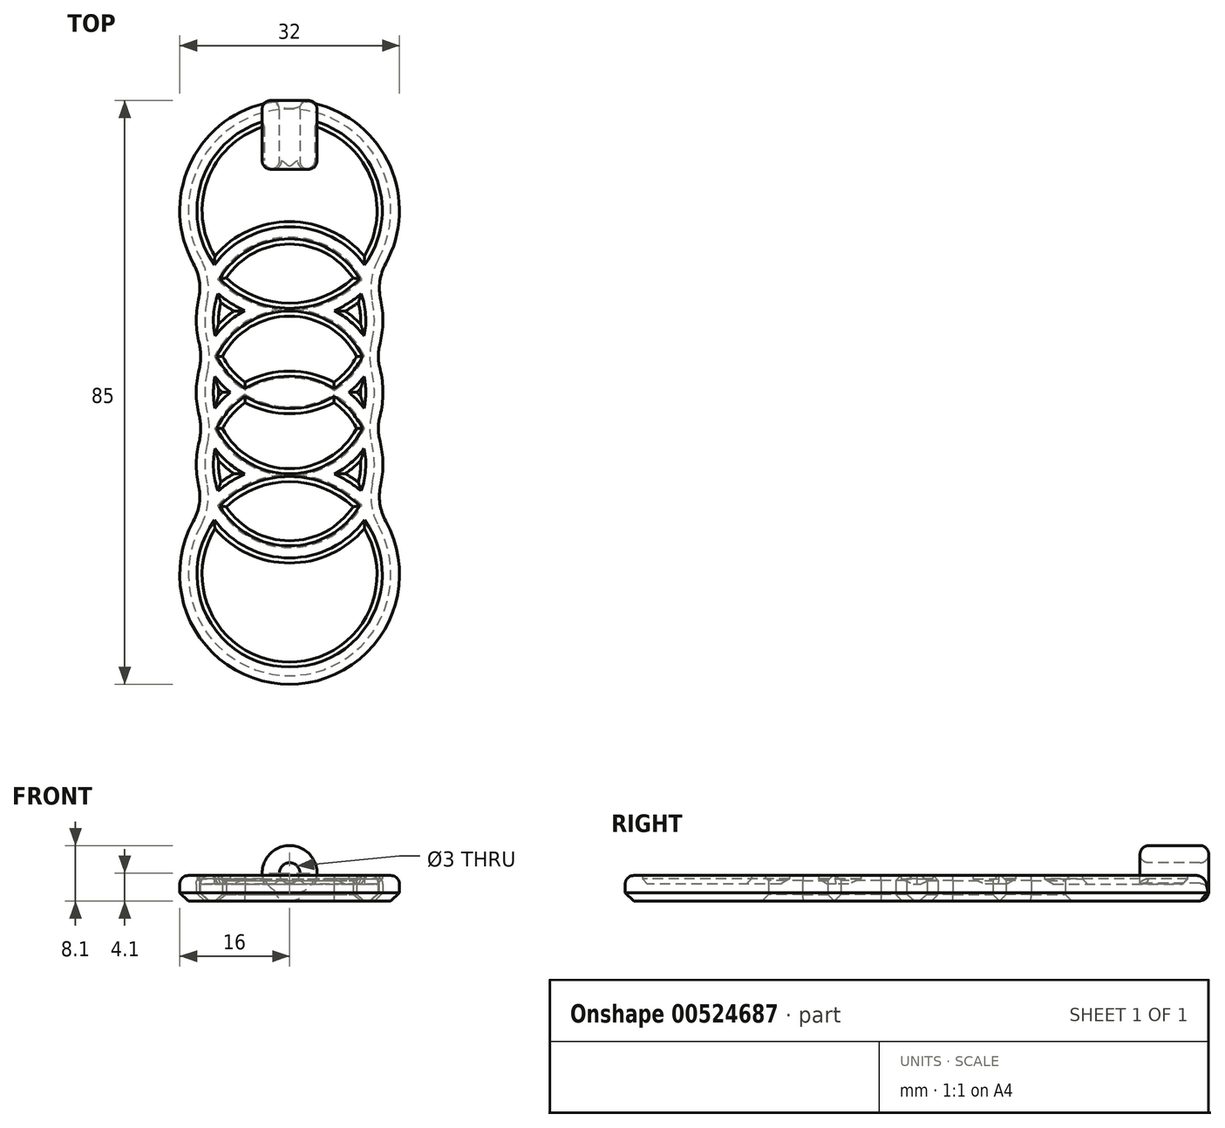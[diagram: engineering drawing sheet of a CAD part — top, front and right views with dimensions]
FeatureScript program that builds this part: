
annotation { "Feature Type Name" : "Feature", "Feature Type Description" : "" }
export const myFeature = defineFeature(function(context is Context, id is Id, definition is map)
    precondition{}
    {
        {
            assignVariable(context, id + "F0", {"name" : "thickness", "anyValue" : 2.5});
        }
        {
            assignVariable(context, id + "F1", {"name" : "handle_length", "anyValue" : 85});
        }
        {
            var Q0;
            Q0=qCreatedBy(makeId("Top.planeOp"),FACE);
            var sketch = newSketch(context, id + "F2", { "sketchPlane" : qUnion([Q0])});
            skLineSegment(sketch, "E0", {"start": v(0, -26.5) * mm, "end": v(0, 26.5) * mm, "construction": true});
            skCircle(sketch, "E1", {"center": v(0, 26.5) * mm, "radius": 16 * mm});
            skCircle(sketch, "E2", {"center": v(0, -26.5) * mm, "radius": 16 * mm});
            skCircle(sketch, "E3", {"center": v(0, 10.5) * mm, "radius": 13.6 * mm});
            skCircle(sketch, "E4", {"center": v(0, -10.5) * mm, "radius": 13.6 * mm});
            skCircle(sketch, "E5", {"center": v(0, 0) * mm, "radius": 13.6 * mm});
            skCircle(sketch, "E6.0", {"center": v(0, 26.5) * mm, "radius": 13.5 * mm});
            skCircle(sketch, "E7.0", {"center": v(0, 10.5) * mm, "radius": 11.1 * mm});
            skCircle(sketch, "E8.0", {"center": v(0, 0) * mm, "radius": 11.1 * mm});
            skCircle(sketch, "E9.0", {"center": v(0, -10.5) * mm, "radius": 11.1 * mm});
            skCircle(sketch, "E10.0", {"center": v(0, -26.5) * mm, "radius": 13.5 * mm});
            skSolve(sketch);
        }
        {
            var Q0;
            Q0=qCreatedBy(makeId("Front.planeOp"),FACE);
            var sketch = newSketch(context, id + "F3", { "sketchPlane" : qUnion([Q0])});
            skLineSegment(sketch, "E11", {"start": v(0, 0) * mm, "end": v(0, 4.1) * mm});
            skCircle(sketch, "E12", {"center": v(0, 4.1) * mm, "radius": 1.5 * mm});
            skCircle(sketch, "E13.0", {"center": v(0, 4.1) * mm, "radius": 4 * mm});
            skSolve(sketch);
        }
        {
            var Q0;
            {var subQ0=sQuery(id+"F2.wireOp",EDGE,"E4");var subQ1=sQuery(id+"F2.wireOp",EDGE,"E2");var subQ2=makeQuery(id+"F2.imprint","INTERSECT",VERTEX,{"disambiguationData":[OD(0.0)],"derivedFrom":[subQ1,subQ0]});Q0=makeQuery(id+"F2.imprint","IMPRINT",FACE,{"disambiguationData":[TD([[makeQuery(id+"F2.imprint","IMPRINT",EDGE,{"disambiguationData":[TD([[subQ2,-1.0]])],"derivedFrom":subQ1}),1.0]])]});}
            var Q1;
            {var subQ0=sQuery(id+"F2.wireOp",EDGE,"E4");var subQ1=sQuery(id+"F2.wireOp",EDGE,"E2");var subQ2=makeQuery(id+"F2.imprint","INTERSECT",VERTEX,{"disambiguationData":[OD(0.0)],"derivedFrom":[subQ1,subQ0]});Q1=makeQuery(id+"F2.imprint","IMPRINT",FACE,{"disambiguationData":[TD([[makeQuery(id+"F2.imprint","IMPRINT",EDGE,{"disambiguationData":[TD([[subQ2,1.0]])],"derivedFrom":subQ1}),1.0]])]});}
            var Q2;
            {var subQ0=sQuery(id+"F2.wireOp",EDGE,"E4");var subQ1=sQuery(id+"F2.wireOp",EDGE,"E2");var subQ2=makeQuery(id+"F2.imprint","INTERSECT",VERTEX,{"disambiguationData":[OD(0.0)],"derivedFrom":[subQ1,subQ0]});Q2=makeQuery(id+"F2.imprint","IMPRINT",FACE,{"disambiguationData":[TD([[makeQuery(id+"F2.imprint","IMPRINT",EDGE,{"disambiguationData":[TD([[subQ2,1.0]])],"derivedFrom":subQ1}),-1.0]])]});}
            var Q3;
            {var subQ0=sQuery(id+"F2.wireOp",EDGE,"E5");var subQ1=sQuery(id+"F2.wireOp",EDGE,"E4");var subQ2=makeQuery(id+"F2.imprint","INTERSECT",VERTEX,{"disambiguationData":[OD(0.0)],"derivedFrom":[subQ1,subQ0]});Q3=makeQuery(id+"F2.imprint","IMPRINT",FACE,{"disambiguationData":[TD([[makeQuery(id+"F2.imprint","IMPRINT",EDGE,{"disambiguationData":[TD([[subQ2,1.0]])],"derivedFrom":subQ1}),1.0]])]});}
            var Q4;
            {var subQ0=sQuery(id+"F2.wireOp",EDGE,"E5");var subQ1=sQuery(id+"F2.wireOp",EDGE,"E3");var subQ2=makeQuery(id+"F2.imprint","INTERSECT",VERTEX,{"disambiguationData":[OD(0.0)],"derivedFrom":[subQ1,subQ0]});Q4=makeQuery(id+"F2.imprint","IMPRINT",FACE,{"disambiguationData":[TD([[makeQuery(id+"F2.imprint","IMPRINT",EDGE,{"disambiguationData":[TD([[subQ2,-1.0]])],"derivedFrom":subQ1}),-1.0]])]});}
            var Q5;
            {var subQ0=sQuery(id+"F2.wireOp",EDGE,"E5");var subQ1=sQuery(id+"F2.wireOp",EDGE,"E3");var subQ2=makeQuery(id+"F2.imprint","INTERSECT",VERTEX,{"disambiguationData":[OD(0.0)],"derivedFrom":[subQ1,subQ0]});Q5=makeQuery(id+"F2.imprint","IMPRINT",FACE,{"disambiguationData":[TD([[makeQuery(id+"F2.imprint","IMPRINT",EDGE,{"disambiguationData":[TD([[subQ2,-1.0]])],"derivedFrom":subQ1}),1.0]])]});}
            var Q6;
            {var subQ0=sQuery(id+"F2.wireOp",EDGE,"E3");var subQ1=sQuery(id+"F2.wireOp",EDGE,"E1");var subQ2=makeQuery(id+"F2.imprint","INTERSECT",VERTEX,{"disambiguationData":[OD(0.0)],"derivedFrom":[subQ1,subQ0]});Q6=makeQuery(id+"F2.imprint","IMPRINT",FACE,{"disambiguationData":[TD([[makeQuery(id+"F2.imprint","IMPRINT",EDGE,{"disambiguationData":[TD([[subQ2,-1.0]])],"derivedFrom":subQ1}),-1.0]])]});}
            var Q7;
            {var subQ0=sQuery(id+"F2.wireOp",EDGE,"E3");var subQ1=sQuery(id+"F2.wireOp",EDGE,"E1");var subQ2=makeQuery(id+"F2.imprint","INTERSECT",VERTEX,{"disambiguationData":[OD(0.0)],"derivedFrom":[subQ1,subQ0]});Q7=makeQuery(id+"F2.imprint","IMPRINT",FACE,{"disambiguationData":[TD([[makeQuery(id+"F2.imprint","IMPRINT",EDGE,{"disambiguationData":[TD([[subQ2,-1.0]])],"derivedFrom":subQ1}),1.0]])]});}
            var Q8;
            {var subQ0=sQuery(id+"F2.wireOp",EDGE,"E3");var subQ1=sQuery(id+"F2.wireOp",EDGE,"E1");var subQ2=makeQuery(id+"F2.imprint","INTERSECT",VERTEX,{"disambiguationData":[OD(0.0)],"derivedFrom":[subQ1,subQ0]});Q8=makeQuery(id+"F2.imprint","IMPRINT",FACE,{"disambiguationData":[TD([[makeQuery(id+"F2.imprint","IMPRINT",EDGE,{"disambiguationData":[TD([[subQ2,1.0]])],"derivedFrom":subQ1}),1.0]])]});}
            var Q9;
            {var subQ0=sQuery(id+"F2.wireOp",EDGE,"E6.0");var subQ1=sQuery(id+"F2.wireOp",EDGE,"E3");var subQ2=makeQuery(id+"F2.imprint","INTERSECT",VERTEX,{"disambiguationData":[OD(0.0)],"derivedFrom":[subQ1,subQ0]});Q9=makeQuery(id+"F2.imprint","IMPRINT",FACE,{"disambiguationData":[TD([[makeQuery(id+"F2.imprint","IMPRINT",EDGE,{"disambiguationData":[TD([[subQ2,-1.0]])],"derivedFrom":subQ1}),-1.0]])]});}
            var Q10;
            {var subQ0=sQuery(id+"F2.wireOp",EDGE,"E10.0");var subQ1=sQuery(id+"F2.wireOp",EDGE,"E4");var subQ2=makeQuery(id+"F2.imprint","INTERSECT",VERTEX,{"disambiguationData":[OD(0.0)],"derivedFrom":[subQ1,subQ0]});Q10=makeQuery(id+"F2.imprint","IMPRINT",FACE,{"disambiguationData":[TD([[makeQuery(id+"F2.imprint","IMPRINT",EDGE,{"disambiguationData":[TD([[subQ2,-1.0]])],"derivedFrom":subQ1}),-1.0]])]});}
            var Q11;
            {var subQ0=sQuery(id+"F2.wireOp",EDGE,"E10.0");var subQ1=sQuery(id+"F2.wireOp",EDGE,"E4");var subQ2=makeQuery(id+"F2.imprint","INTERSECT",VERTEX,{"disambiguationData":[OD(0.0)],"derivedFrom":[subQ1,subQ0]});Q11=makeQuery(id+"F2.imprint","IMPRINT",FACE,{"disambiguationData":[TD([[makeQuery(id+"F2.imprint","IMPRINT",EDGE,{"disambiguationData":[TD([[subQ2,-1.0]])],"derivedFrom":subQ1}),1.0]])]});}
            var Q12;
            {var subQ0=sQuery(id+"F2.wireOp",EDGE,"E4");var subQ1=sQuery(id+"F2.wireOp",EDGE,"E2");var subQ2=makeQuery(id+"F2.imprint","INTERSECT",VERTEX,{"disambiguationData":[OD(1.0)],"derivedFrom":[subQ1,subQ0]});Q12=makeQuery(id+"F2.imprint","IMPRINT",FACE,{"disambiguationData":[TD([[makeQuery(id+"F2.imprint","IMPRINT",EDGE,{"disambiguationData":[TD([[subQ2,1.0]])],"derivedFrom":subQ1}),1.0]])]});}
            var Q13;
            {var subQ0=sQuery(id+"F2.wireOp",EDGE,"E9.0");var subQ1=sQuery(id+"F2.wireOp",EDGE,"E2");var subQ2=makeQuery(id+"F2.imprint","INTERSECT",VERTEX,{"disambiguationData":[OD(0.0)],"derivedFrom":[subQ1,subQ0]});Q13=makeQuery(id+"F2.imprint","IMPRINT",FACE,{"disambiguationData":[TD([[makeQuery(id+"F2.imprint","IMPRINT",EDGE,{"disambiguationData":[TD([[subQ2,-1.0]])],"derivedFrom":subQ1}),1.0]])]});}
            var Q14;
            {var subQ0=sQuery(id+"F2.wireOp",EDGE,"E9.0");var subQ1=sQuery(id+"F2.wireOp",EDGE,"E5");var subQ2=makeQuery(id+"F2.imprint","INTERSECT",VERTEX,{"disambiguationData":[OD(0.0)],"derivedFrom":[subQ1,subQ0]});Q14=makeQuery(id+"F2.imprint","IMPRINT",FACE,{"disambiguationData":[TD([[makeQuery(id+"F2.imprint","IMPRINT",EDGE,{"disambiguationData":[TD([[subQ2,-1.0]])],"derivedFrom":subQ1}),1.0]])]});}
            var Q15;
            {var subQ0=sQuery(id+"F2.wireOp",EDGE,"E4");var subQ1=sQuery(id+"F2.wireOp",EDGE,"E2");var subQ2=makeQuery(id+"F2.imprint","INTERSECT",VERTEX,{"disambiguationData":[OD(1.0)],"derivedFrom":[subQ1,subQ0]});Q15=makeQuery(id+"F2.imprint","IMPRINT",FACE,{"disambiguationData":[TD([[makeQuery(id+"F2.imprint","IMPRINT",EDGE,{"disambiguationData":[TD([[subQ2,1.0]])],"derivedFrom":subQ1}),-1.0]])]});}
            var Q16;
            {var subQ0=sQuery(id+"F2.wireOp",EDGE,"E5");var subQ1=sQuery(id+"F2.wireOp",EDGE,"E4");var subQ2=makeQuery(id+"F2.imprint","INTERSECT",VERTEX,{"disambiguationData":[OD(1.0)],"derivedFrom":[subQ1,subQ0]});Q16=makeQuery(id+"F2.imprint","IMPRINT",FACE,{"disambiguationData":[TD([[makeQuery(id+"F2.imprint","IMPRINT",EDGE,{"disambiguationData":[TD([[subQ2,1.0]])],"derivedFrom":subQ1}),1.0]])]});}
            var Q17;
            {var subQ0=sQuery(id+"F2.wireOp",EDGE,"E8.0");var subQ1=sQuery(id+"F2.wireOp",EDGE,"E4");var subQ2=makeQuery(id+"F2.imprint","INTERSECT",VERTEX,{"disambiguationData":[OD(0.0)],"derivedFrom":[subQ1,subQ0]});Q17=makeQuery(id+"F2.imprint","IMPRINT",FACE,{"disambiguationData":[TD([[makeQuery(id+"F2.imprint","IMPRINT",EDGE,{"disambiguationData":[TD([[subQ2,-1.0]])],"derivedFrom":subQ1}),1.0]])]});}
            var Q18;
            {var subQ0=sQuery(id+"F2.wireOp",EDGE,"E5");var subQ1=sQuery(id+"F2.wireOp",EDGE,"E3");var subQ2=makeQuery(id+"F2.imprint","INTERSECT",VERTEX,{"disambiguationData":[OD(1.0)],"derivedFrom":[subQ1,subQ0]});Q18=makeQuery(id+"F2.imprint","IMPRINT",FACE,{"disambiguationData":[TD([[makeQuery(id+"F2.imprint","IMPRINT",EDGE,{"disambiguationData":[TD([[subQ2,1.0]])],"derivedFrom":subQ1}),-1.0]])]});}
            var Q19;
            {var subQ0=sQuery(id+"F2.wireOp",EDGE,"E5");var subQ1=sQuery(id+"F2.wireOp",EDGE,"E4");var subQ2=makeQuery(id+"F2.imprint","INTERSECT",VERTEX,{"disambiguationData":[OD(0.0)],"derivedFrom":[subQ1,subQ0]});Q19=makeQuery(id+"F2.imprint","IMPRINT",FACE,{"disambiguationData":[TD([[makeQuery(id+"F2.imprint","IMPRINT",EDGE,{"disambiguationData":[TD([[subQ2,-1.0]])],"derivedFrom":subQ1}),1.0]])]});}
            var Q20;
            {var subQ0=sQuery(id+"F2.wireOp",EDGE,"E8.0");var subQ1=sQuery(id+"F2.wireOp",EDGE,"E3");var subQ2=makeQuery(id+"F2.imprint","INTERSECT",VERTEX,{"disambiguationData":[OD(0.0)],"derivedFrom":[subQ1,subQ0]});Q20=makeQuery(id+"F2.imprint","IMPRINT",FACE,{"disambiguationData":[TD([[makeQuery(id+"F2.imprint","IMPRINT",EDGE,{"disambiguationData":[TD([[subQ2,-1.0]])],"derivedFrom":subQ1}),1.0]])]});}
            var Q21;
            {var subQ0=sQuery(id+"F2.wireOp",EDGE,"E5");var subQ1=sQuery(id+"F2.wireOp",EDGE,"E3");var subQ2=makeQuery(id+"F2.imprint","INTERSECT",VERTEX,{"disambiguationData":[OD(1.0)],"derivedFrom":[subQ1,subQ0]});Q21=makeQuery(id+"F2.imprint","IMPRINT",FACE,{"disambiguationData":[TD([[makeQuery(id+"F2.imprint","IMPRINT",EDGE,{"disambiguationData":[TD([[subQ2,1.0]])],"derivedFrom":subQ1}),1.0]])]});}
            var Q22;
            {var subQ0=sQuery(id+"F2.wireOp",EDGE,"E3");var subQ1=sQuery(id+"F2.wireOp",EDGE,"E1");var subQ2=makeQuery(id+"F2.imprint","INTERSECT",VERTEX,{"disambiguationData":[OD(1.0)],"derivedFrom":[subQ1,subQ0]});Q22=makeQuery(id+"F2.imprint","IMPRINT",FACE,{"disambiguationData":[TD([[makeQuery(id+"F2.imprint","IMPRINT",EDGE,{"disambiguationData":[TD([[subQ2,1.0]])],"derivedFrom":subQ1}),-1.0]])]});}
            var Q23;
            {var subQ0=sQuery(id+"F2.wireOp",EDGE,"E7.0");var subQ1=sQuery(id+"F2.wireOp",EDGE,"E5");var subQ2=makeQuery(id+"F2.imprint","INTERSECT",VERTEX,{"disambiguationData":[OD(0.0)],"derivedFrom":[subQ1,subQ0]});Q23=makeQuery(id+"F2.imprint","IMPRINT",FACE,{"disambiguationData":[TD([[makeQuery(id+"F2.imprint","IMPRINT",EDGE,{"disambiguationData":[TD([[subQ2,-1.0]])],"derivedFrom":subQ1}),1.0]])]});}
            var Q24;
            {var subQ0=sQuery(id+"F2.wireOp",EDGE,"E7.0");var subQ1=sQuery(id+"F2.wireOp",EDGE,"E1");var subQ2=makeQuery(id+"F2.imprint","INTERSECT",VERTEX,{"disambiguationData":[OD(0.0)],"derivedFrom":[subQ1,subQ0]});Q24=makeQuery(id+"F2.imprint","IMPRINT",FACE,{"disambiguationData":[TD([[makeQuery(id+"F2.imprint","IMPRINT",EDGE,{"disambiguationData":[TD([[subQ2,-1.0]])],"derivedFrom":subQ1}),1.0]])]});}
            var Q25;
            {var subQ0=sQuery(id+"F2.wireOp",EDGE,"E6.0");var subQ1=sQuery(id+"F2.wireOp",EDGE,"E3");var subQ2=makeQuery(id+"F2.imprint","INTERSECT",VERTEX,{"disambiguationData":[OD(0.0)],"derivedFrom":[subQ1,subQ0]});Q25=makeQuery(id+"F2.imprint","IMPRINT",FACE,{"disambiguationData":[TD([[makeQuery(id+"F2.imprint","IMPRINT",EDGE,{"disambiguationData":[TD([[subQ2,-1.0]])],"derivedFrom":subQ1}),1.0]])]});}
            var Q26;
            {var subQ0=sQuery(id+"F2.wireOp",EDGE,"E3");var subQ1=sQuery(id+"F2.wireOp",EDGE,"E1");var subQ2=makeQuery(id+"F2.imprint","INTERSECT",VERTEX,{"disambiguationData":[OD(1.0)],"derivedFrom":[subQ1,subQ0]});Q26=makeQuery(id+"F2.imprint","IMPRINT",FACE,{"disambiguationData":[TD([[makeQuery(id+"F2.imprint","IMPRINT",EDGE,{"disambiguationData":[TD([[subQ2,1.0]])],"derivedFrom":subQ1}),1.0]])]});}
            var Q27;
            {var subQ0=sQuery(id+"F2.wireOp",EDGE,"E5");var subQ1=sQuery(id+"F2.wireOp",EDGE,"E2");var subQ2=makeQuery(id+"F2.imprint","INTERSECT",VERTEX,{"disambiguationData":[OD(0.0)],"derivedFrom":[subQ1,subQ0]});Q27=makeQuery(id+"F2.imprint","IMPRINT",FACE,{"disambiguationData":[TD([[makeQuery(id+"F2.imprint","IMPRINT",EDGE,{"disambiguationData":[TD([[subQ2,-1.0]])],"derivedFrom":subQ1}),1.0]])]});}
            var Q28;
            {var subQ0=sQuery(id+"F2.wireOp",EDGE,"E5");var subQ1=sQuery(id+"F2.wireOp",EDGE,"E2");var subQ2=makeQuery(id+"F2.imprint","INTERSECT",VERTEX,{"disambiguationData":[OD(0.0)],"derivedFrom":[subQ1,subQ0]});Q28=makeQuery(id+"F2.imprint","IMPRINT",FACE,{"disambiguationData":[TD([[makeQuery(id+"F2.imprint","IMPRINT",EDGE,{"disambiguationData":[TD([[subQ2,-1.0]])],"derivedFrom":subQ1}),-1.0]])]});}
            var Q29;
            {var subQ0=sQuery(id+"F2.wireOp",EDGE,"E5");var subQ1=sQuery(id+"F2.wireOp",EDGE,"E2");var subQ2=makeQuery(id+"F2.imprint","INTERSECT",VERTEX,{"disambiguationData":[OD(1.0)],"derivedFrom":[subQ1,subQ0]});Q29=makeQuery(id+"F2.imprint","IMPRINT",FACE,{"disambiguationData":[TD([[makeQuery(id+"F2.imprint","IMPRINT",EDGE,{"disambiguationData":[TD([[subQ2,-1.0]])],"derivedFrom":subQ1}),1.0]])]});}
            var Q30;
            {var subQ0=sQuery(id+"F2.wireOp",EDGE,"E9.0");var subQ1=sQuery(id+"F2.wireOp",EDGE,"E3");var subQ2=makeQuery(id+"F2.imprint","INTERSECT",VERTEX,{"disambiguationData":[OD(1.0)],"derivedFrom":[subQ1,subQ0]});Q30=makeQuery(id+"F2.imprint","IMPRINT",FACE,{"disambiguationData":[TD([[makeQuery(id+"F2.imprint","IMPRINT",EDGE,{"disambiguationData":[TD([[subQ2,-1.0]])],"derivedFrom":subQ1}),1.0]])]});}
            var Q31;
            {var subQ0=sQuery(id+"F2.wireOp",EDGE,"E4");var subQ1=sQuery(id+"F2.wireOp",EDGE,"E3");var subQ2=makeQuery(id+"F2.imprint","INTERSECT",VERTEX,{"disambiguationData":[OD(1.0)],"derivedFrom":[subQ1,subQ0]});Q31=makeQuery(id+"F2.imprint","IMPRINT",FACE,{"disambiguationData":[TD([[makeQuery(id+"F2.imprint","IMPRINT",EDGE,{"disambiguationData":[TD([[subQ2,-1.0]])],"derivedFrom":subQ1}),1.0]])]});}
            var Q32;
            {var subQ0=sQuery(id+"F2.wireOp",EDGE,"E7.0");var subQ1=sQuery(id+"F2.wireOp",EDGE,"E4");var subQ2=makeQuery(id+"F2.imprint","INTERSECT",VERTEX,{"disambiguationData":[OD(0.0)],"derivedFrom":[subQ1,subQ0]});Q32=makeQuery(id+"F2.imprint","IMPRINT",FACE,{"disambiguationData":[TD([[makeQuery(id+"F2.imprint","IMPRINT",EDGE,{"disambiguationData":[TD([[subQ2,-1.0]])],"derivedFrom":subQ1}),1.0]])]});}
            var Q33;
            {var subQ0=sQuery(id+"F2.wireOp",EDGE,"E9.0");var subQ1=sQuery(id+"F2.wireOp",EDGE,"E3");var subQ2=makeQuery(id+"F2.imprint","INTERSECT",VERTEX,{"disambiguationData":[OD(0.0)],"derivedFrom":[subQ1,subQ0]});Q33=makeQuery(id+"F2.imprint","IMPRINT",FACE,{"disambiguationData":[TD([[makeQuery(id+"F2.imprint","IMPRINT",EDGE,{"disambiguationData":[TD([[subQ2,-1.0]])],"derivedFrom":subQ1}),1.0]])]});}
            var Q34;
            {var subQ0=sQuery(id+"F2.wireOp",EDGE,"E4");var subQ1=sQuery(id+"F2.wireOp",EDGE,"E3");var subQ2=makeQuery(id+"F2.imprint","INTERSECT",VERTEX,{"disambiguationData":[OD(0.0)],"derivedFrom":[subQ1,subQ0]});Q34=makeQuery(id+"F2.imprint","IMPRINT",FACE,{"disambiguationData":[TD([[makeQuery(id+"F2.imprint","IMPRINT",EDGE,{"disambiguationData":[TD([[subQ2,-1.0]])],"derivedFrom":subQ1}),1.0]])]});}
            var Q35;
            {var subQ0=sQuery(id+"F2.wireOp",EDGE,"E5");var subQ1=sQuery(id+"F2.wireOp",EDGE,"E1");var subQ2=makeQuery(id+"F2.imprint","INTERSECT",VERTEX,{"disambiguationData":[OD(1.0)],"derivedFrom":[subQ1,subQ0]});Q35=makeQuery(id+"F2.imprint","IMPRINT",FACE,{"disambiguationData":[TD([[makeQuery(id+"F2.imprint","IMPRINT",EDGE,{"disambiguationData":[TD([[subQ2,-1.0]])],"derivedFrom":subQ1}),1.0]])]});}
            var Q36;
            {var subQ0=sQuery(id+"F2.wireOp",EDGE,"E5");var subQ1=sQuery(id+"F2.wireOp",EDGE,"E1");var subQ2=makeQuery(id+"F2.imprint","INTERSECT",VERTEX,{"disambiguationData":[OD(0.0)],"derivedFrom":[subQ1,subQ0]});Q36=makeQuery(id+"F2.imprint","IMPRINT",FACE,{"disambiguationData":[TD([[makeQuery(id+"F2.imprint","IMPRINT",EDGE,{"disambiguationData":[TD([[subQ2,-1.0]])],"derivedFrom":subQ1}),1.0]])]});}
            var Q37;
            {var subQ0=sQuery(id+"F2.wireOp",EDGE,"E5");var subQ1=sQuery(id+"F2.wireOp",EDGE,"E1");var subQ2=makeQuery(id+"F2.imprint","INTERSECT",VERTEX,{"disambiguationData":[OD(0.0)],"derivedFrom":[subQ1,subQ0]});Q37=makeQuery(id+"F2.imprint","IMPRINT",FACE,{"disambiguationData":[TD([[makeQuery(id+"F2.imprint","IMPRINT",EDGE,{"disambiguationData":[TD([[subQ2,-1.0]])],"derivedFrom":subQ1}),-1.0]])]});}
            var Q38;
            {var subQ0=sQuery(id+"F2.wireOp",EDGE,"E4");var subQ1=sQuery(id+"F2.wireOp",EDGE,"E3");var subQ2=makeQuery(id+"F2.imprint","INTERSECT",VERTEX,{"disambiguationData":[OD(0.0)],"derivedFrom":[subQ1,subQ0]});Q38=makeQuery(id+"F2.imprint","IMPRINT",FACE,{"disambiguationData":[TD([[makeQuery(id+"F2.imprint","IMPRINT",EDGE,{"disambiguationData":[TD([[subQ2,-1.0]])],"derivedFrom":subQ1}),-1.0]])]});}
            var Q39;
            {var subQ0=sQuery(id+"F2.wireOp",EDGE,"E5");var subQ1=sQuery(id+"F2.wireOp",EDGE,"E2");var subQ2=makeQuery(id+"F2.imprint","INTERSECT",VERTEX,{"disambiguationData":[OD(1.0)],"derivedFrom":[subQ1,subQ0]});Q39=makeQuery(id+"F2.imprint","IMPRINT",FACE,{"disambiguationData":[TD([[makeQuery(id+"F2.imprint","IMPRINT",EDGE,{"disambiguationData":[TD([[subQ2,-1.0]])],"derivedFrom":subQ1}),-1.0]])]});}
            var Q40;
            {var subQ0=sQuery(id+"F2.wireOp",EDGE,"E9.0");var subQ1=sQuery(id+"F2.wireOp",EDGE,"E2");var subQ2=makeQuery(id+"F2.imprint","INTERSECT",VERTEX,{"disambiguationData":[OD(0.0)],"derivedFrom":[subQ1,subQ0]});Q40=makeQuery(id+"F2.imprint","IMPRINT",FACE,{"disambiguationData":[TD([[makeQuery(id+"F2.imprint","IMPRINT",EDGE,{"disambiguationData":[TD([[subQ2,-1.0]])],"derivedFrom":subQ1}),-1.0]])]});}
            var Q41;
            {var subQ0=sQuery(id+"F2.wireOp",EDGE,"E8.0");var subQ1=sQuery(id+"F2.wireOp",EDGE,"E3");var subQ2=makeQuery(id+"F2.imprint","INTERSECT",VERTEX,{"disambiguationData":[OD(0.0)],"derivedFrom":[subQ1,subQ0]});Q41=makeQuery(id+"F2.imprint","IMPRINT",FACE,{"disambiguationData":[TD([[makeQuery(id+"F2.imprint","IMPRINT",EDGE,{"disambiguationData":[TD([[subQ2,-1.0]])],"derivedFrom":subQ1}),-1.0]])]});}
            var Q42;
            {var subQ0=sQuery(id+"F2.wireOp",EDGE,"E4");var subQ1=sQuery(id+"F2.wireOp",EDGE,"E3");var subQ2=makeQuery(id+"F2.imprint","INTERSECT",VERTEX,{"disambiguationData":[OD(1.0)],"derivedFrom":[subQ1,subQ0]});Q42=makeQuery(id+"F2.imprint","IMPRINT",FACE,{"disambiguationData":[TD([[makeQuery(id+"F2.imprint","IMPRINT",EDGE,{"disambiguationData":[TD([[subQ2,-1.0]])],"derivedFrom":subQ1}),-1.0]])]});}
            var Q43;
            {var subQ0=sQuery(id+"F2.wireOp",EDGE,"E9.0");var subQ1=sQuery(id+"F2.wireOp",EDGE,"E7.0");var subQ2=makeQuery(id+"F2.imprint","INTERSECT",VERTEX,{"disambiguationData":[OD(0.0)],"derivedFrom":[subQ1,subQ0]});Q43=makeQuery(id+"F2.imprint","IMPRINT",FACE,{"disambiguationData":[TD([[makeQuery(id+"F2.imprint","IMPRINT",EDGE,{"disambiguationData":[TD([[subQ2,-1.0]])],"derivedFrom":subQ1}),1.0]])]});}
            var Q44;
            {var subQ0=sQuery(id+"F2.wireOp",EDGE,"E7.0");var subQ1=sQuery(id+"F2.wireOp",EDGE,"E1");var subQ2=makeQuery(id+"F2.imprint","INTERSECT",VERTEX,{"disambiguationData":[OD(0.0)],"derivedFrom":[subQ1,subQ0]});Q44=makeQuery(id+"F2.imprint","IMPRINT",FACE,{"disambiguationData":[TD([[makeQuery(id+"F2.imprint","IMPRINT",EDGE,{"disambiguationData":[TD([[subQ2,-1.0]])],"derivedFrom":subQ1}),-1.0]])]});}
            var Q45;
            {var subQ0=sQuery(id+"F2.wireOp",EDGE,"E5");var subQ1=sQuery(id+"F2.wireOp",EDGE,"E1");var subQ2=makeQuery(id+"F2.imprint","INTERSECT",VERTEX,{"disambiguationData":[OD(1.0)],"derivedFrom":[subQ1,subQ0]});Q45=makeQuery(id+"F2.imprint","IMPRINT",FACE,{"disambiguationData":[TD([[makeQuery(id+"F2.imprint","IMPRINT",EDGE,{"disambiguationData":[TD([[subQ2,-1.0]])],"derivedFrom":subQ1}),-1.0]])]});}
            extrude(context, id + "F4", {"entities" : qUnion([Q0, Q1, Q2, Q3, Q4, Q5, Q6, Q7, Q8, Q9, Q10, Q11, Q12, Q13, Q14, Q15, Q16, Q17, Q18, Q19, Q20, Q21, Q22, Q23, Q24, Q25, Q26, Q27, Q28, Q29, Q30, Q31, Q32, Q33, Q34, Q35, Q36, Q37, Q38, Q39, Q40, Q41, Q42, Q43, Q44, Q45]), "depth" : (getVariable(context, 'thickness')) * mm, "offsetDistance" : 25 * mm});
        }
        {
            var Q0;
            {var subQ0=sQuery(id+"F2.wireOp",EDGE,"E4");var subQ1=sQuery(id+"F2.wireOp",EDGE,"E2");var subQ2=makeQuery(id+"F2.imprint","INTERSECT",VERTEX,{"disambiguationData":[OD(0.0)],"derivedFrom":[subQ1,subQ0]});Q0=makeQuery(id+"F2.imprint","IMPRINT",FACE,{"disambiguationData":[TD([[makeQuery(id+"F2.imprint","IMPRINT",EDGE,{"disambiguationData":[TD([[subQ2,1.0]])],"derivedFrom":subQ1}),1.0]])]});}
            var Q1;
            {var subQ0=sQuery(id+"F2.wireOp",EDGE,"E4");var subQ1=sQuery(id+"F2.wireOp",EDGE,"E2");var subQ2=makeQuery(id+"F2.imprint","INTERSECT",VERTEX,{"disambiguationData":[OD(1.0)],"derivedFrom":[subQ1,subQ0]});Q1=makeQuery(id+"F2.imprint","IMPRINT",FACE,{"disambiguationData":[TD([[makeQuery(id+"F2.imprint","IMPRINT",EDGE,{"disambiguationData":[TD([[subQ2,1.0]])],"derivedFrom":subQ1}),1.0]])]});}
            var Q2;
            {var subQ0=sQuery(id+"F2.wireOp",EDGE,"E10.0");var subQ1=sQuery(id+"F2.wireOp",EDGE,"E4");var subQ2=makeQuery(id+"F2.imprint","INTERSECT",VERTEX,{"disambiguationData":[OD(0.0)],"derivedFrom":[subQ1,subQ0]});Q2=makeQuery(id+"F2.imprint","IMPRINT",FACE,{"disambiguationData":[TD([[makeQuery(id+"F2.imprint","IMPRINT",EDGE,{"disambiguationData":[TD([[subQ2,-1.0]])],"derivedFrom":subQ1}),1.0]])]});}
            var Q3;
            {var subQ0=sQuery(id+"F2.wireOp",EDGE,"E9.0");var subQ1=sQuery(id+"F2.wireOp",EDGE,"E2");var subQ2=makeQuery(id+"F2.imprint","INTERSECT",VERTEX,{"disambiguationData":[OD(0.0)],"derivedFrom":[subQ1,subQ0]});Q3=makeQuery(id+"F2.imprint","IMPRINT",FACE,{"disambiguationData":[TD([[makeQuery(id+"F2.imprint","IMPRINT",EDGE,{"disambiguationData":[TD([[subQ2,-1.0]])],"derivedFrom":subQ1}),1.0]])]});}
            var Q4;
            {var subQ0=sQuery(id+"F2.wireOp",EDGE,"E4");var subQ1=sQuery(id+"F2.wireOp",EDGE,"E2");var subQ2=makeQuery(id+"F2.imprint","INTERSECT",VERTEX,{"disambiguationData":[OD(0.0)],"derivedFrom":[subQ1,subQ0]});Q4=makeQuery(id+"F2.imprint","IMPRINT",FACE,{"disambiguationData":[TD([[makeQuery(id+"F2.imprint","IMPRINT",EDGE,{"disambiguationData":[TD([[subQ2,-1.0]])],"derivedFrom":subQ1}),1.0]])]});}
            var Q5;
            {var subQ0=sQuery(id+"F2.wireOp",EDGE,"E3");var subQ1=sQuery(id+"F2.wireOp",EDGE,"E1");var subQ2=makeQuery(id+"F2.imprint","INTERSECT",VERTEX,{"disambiguationData":[OD(0.0)],"derivedFrom":[subQ1,subQ0]});Q5=makeQuery(id+"F2.imprint","IMPRINT",FACE,{"disambiguationData":[TD([[makeQuery(id+"F2.imprint","IMPRINT",EDGE,{"disambiguationData":[TD([[subQ2,1.0]])],"derivedFrom":subQ1}),1.0]])]});}
            var Q6;
            {var subQ0=sQuery(id+"F2.wireOp",EDGE,"E3");var subQ1=sQuery(id+"F2.wireOp",EDGE,"E1");var subQ2=makeQuery(id+"F2.imprint","INTERSECT",VERTEX,{"disambiguationData":[OD(0.0)],"derivedFrom":[subQ1,subQ0]});Q6=makeQuery(id+"F2.imprint","IMPRINT",FACE,{"disambiguationData":[TD([[makeQuery(id+"F2.imprint","IMPRINT",EDGE,{"disambiguationData":[TD([[subQ2,-1.0]])],"derivedFrom":subQ1}),1.0]])]});}
            var Q7;
            {var subQ0=sQuery(id+"F2.wireOp",EDGE,"E6.0");var subQ1=sQuery(id+"F2.wireOp",EDGE,"E3");var subQ2=makeQuery(id+"F2.imprint","INTERSECT",VERTEX,{"disambiguationData":[OD(0.0)],"derivedFrom":[subQ1,subQ0]});Q7=makeQuery(id+"F2.imprint","IMPRINT",FACE,{"disambiguationData":[TD([[makeQuery(id+"F2.imprint","IMPRINT",EDGE,{"disambiguationData":[TD([[subQ2,-1.0]])],"derivedFrom":subQ1}),1.0]])]});}
            var Q8;
            {var subQ0=sQuery(id+"F2.wireOp",EDGE,"E7.0");var subQ1=sQuery(id+"F2.wireOp",EDGE,"E1");var subQ2=makeQuery(id+"F2.imprint","INTERSECT",VERTEX,{"disambiguationData":[OD(0.0)],"derivedFrom":[subQ1,subQ0]});Q8=makeQuery(id+"F2.imprint","IMPRINT",FACE,{"disambiguationData":[TD([[makeQuery(id+"F2.imprint","IMPRINT",EDGE,{"disambiguationData":[TD([[subQ2,-1.0]])],"derivedFrom":subQ1}),1.0]])]});}
            var Q9;
            {var subQ0=sQuery(id+"F2.wireOp",EDGE,"E3");var subQ1=sQuery(id+"F2.wireOp",EDGE,"E1");var subQ2=makeQuery(id+"F2.imprint","INTERSECT",VERTEX,{"disambiguationData":[OD(1.0)],"derivedFrom":[subQ1,subQ0]});Q9=makeQuery(id+"F2.imprint","IMPRINT",FACE,{"disambiguationData":[TD([[makeQuery(id+"F2.imprint","IMPRINT",EDGE,{"disambiguationData":[TD([[subQ2,1.0]])],"derivedFrom":subQ1}),-1.0]])]});}
            var Q10;
            {var subQ0=sQuery(id+"F2.wireOp",EDGE,"E3");var subQ1=sQuery(id+"F2.wireOp",EDGE,"E1");var subQ2=makeQuery(id+"F2.imprint","INTERSECT",VERTEX,{"disambiguationData":[OD(1.0)],"derivedFrom":[subQ1,subQ0]});Q10=makeQuery(id+"F2.imprint","IMPRINT",FACE,{"disambiguationData":[TD([[makeQuery(id+"F2.imprint","IMPRINT",EDGE,{"disambiguationData":[TD([[subQ2,1.0]])],"derivedFrom":subQ1}),1.0]])]});}
            var Q11;
            {var subQ0=sQuery(id+"F2.wireOp",EDGE,"E7.0");var subQ1=sQuery(id+"F2.wireOp",EDGE,"E5");var subQ2=makeQuery(id+"F2.imprint","INTERSECT",VERTEX,{"disambiguationData":[OD(0.0)],"derivedFrom":[subQ1,subQ0]});Q11=makeQuery(id+"F2.imprint","IMPRINT",FACE,{"disambiguationData":[TD([[makeQuery(id+"F2.imprint","IMPRINT",EDGE,{"disambiguationData":[TD([[subQ2,-1.0]])],"derivedFrom":subQ1}),1.0]])]});}
            var Q12;
            {var subQ0=sQuery(id+"F2.wireOp",EDGE,"E5");var subQ1=sQuery(id+"F2.wireOp",EDGE,"E3");var subQ2=makeQuery(id+"F2.imprint","INTERSECT",VERTEX,{"disambiguationData":[OD(1.0)],"derivedFrom":[subQ1,subQ0]});Q12=makeQuery(id+"F2.imprint","IMPRINT",FACE,{"disambiguationData":[TD([[makeQuery(id+"F2.imprint","IMPRINT",EDGE,{"disambiguationData":[TD([[subQ2,1.0]])],"derivedFrom":subQ1}),1.0]])]});}
            var Q13;
            {var subQ0=sQuery(id+"F2.wireOp",EDGE,"E8.0");var subQ1=sQuery(id+"F2.wireOp",EDGE,"E3");var subQ2=makeQuery(id+"F2.imprint","INTERSECT",VERTEX,{"disambiguationData":[OD(0.0)],"derivedFrom":[subQ1,subQ0]});Q13=makeQuery(id+"F2.imprint","IMPRINT",FACE,{"disambiguationData":[TD([[makeQuery(id+"F2.imprint","IMPRINT",EDGE,{"disambiguationData":[TD([[subQ2,-1.0]])],"derivedFrom":subQ1}),1.0]])]});}
            var Q14;
            {var subQ0=sQuery(id+"F2.wireOp",EDGE,"E5");var subQ1=sQuery(id+"F2.wireOp",EDGE,"E3");var subQ2=makeQuery(id+"F2.imprint","INTERSECT",VERTEX,{"disambiguationData":[OD(0.0)],"derivedFrom":[subQ1,subQ0]});Q14=makeQuery(id+"F2.imprint","IMPRINT",FACE,{"disambiguationData":[TD([[makeQuery(id+"F2.imprint","IMPRINT",EDGE,{"disambiguationData":[TD([[subQ2,-1.0]])],"derivedFrom":subQ1}),1.0]])]});}
            var Q15;
            {var subQ0=sQuery(id+"F2.wireOp",EDGE,"E3");var subQ1=sQuery(id+"F2.wireOp",EDGE,"E1");var subQ2=makeQuery(id+"F2.imprint","INTERSECT",VERTEX,{"disambiguationData":[OD(0.0)],"derivedFrom":[subQ1,subQ0]});Q15=makeQuery(id+"F2.imprint","IMPRINT",FACE,{"disambiguationData":[TD([[makeQuery(id+"F2.imprint","IMPRINT",EDGE,{"disambiguationData":[TD([[subQ2,-1.0]])],"derivedFrom":subQ1}),-1.0]])]});}
            var Q16;
            {var subQ0=sQuery(id+"F2.wireOp",EDGE,"E5");var subQ1=sQuery(id+"F2.wireOp",EDGE,"E3");var subQ2=makeQuery(id+"F2.imprint","INTERSECT",VERTEX,{"disambiguationData":[OD(0.0)],"derivedFrom":[subQ1,subQ0]});Q16=makeQuery(id+"F2.imprint","IMPRINT",FACE,{"disambiguationData":[TD([[makeQuery(id+"F2.imprint","IMPRINT",EDGE,{"disambiguationData":[TD([[subQ2,-1.0]])],"derivedFrom":subQ1}),-1.0]])]});}
            var Q17;
            {var subQ0=sQuery(id+"F2.wireOp",EDGE,"E5");var subQ1=sQuery(id+"F2.wireOp",EDGE,"E4");var subQ2=makeQuery(id+"F2.imprint","INTERSECT",VERTEX,{"disambiguationData":[OD(1.0)],"derivedFrom":[subQ1,subQ0]});Q17=makeQuery(id+"F2.imprint","IMPRINT",FACE,{"disambiguationData":[TD([[makeQuery(id+"F2.imprint","IMPRINT",EDGE,{"disambiguationData":[TD([[subQ2,1.0]])],"derivedFrom":subQ1}),1.0]])]});}
            var Q18;
            {var subQ0=sQuery(id+"F2.wireOp",EDGE,"E8.0");var subQ1=sQuery(id+"F2.wireOp",EDGE,"E4");var subQ2=makeQuery(id+"F2.imprint","INTERSECT",VERTEX,{"disambiguationData":[OD(0.0)],"derivedFrom":[subQ1,subQ0]});Q18=makeQuery(id+"F2.imprint","IMPRINT",FACE,{"disambiguationData":[TD([[makeQuery(id+"F2.imprint","IMPRINT",EDGE,{"disambiguationData":[TD([[subQ2,-1.0]])],"derivedFrom":subQ1}),1.0]])]});}
            var Q19;
            {var subQ0=sQuery(id+"F2.wireOp",EDGE,"E9.0");var subQ1=sQuery(id+"F2.wireOp",EDGE,"E5");var subQ2=makeQuery(id+"F2.imprint","INTERSECT",VERTEX,{"disambiguationData":[OD(0.0)],"derivedFrom":[subQ1,subQ0]});Q19=makeQuery(id+"F2.imprint","IMPRINT",FACE,{"disambiguationData":[TD([[makeQuery(id+"F2.imprint","IMPRINT",EDGE,{"disambiguationData":[TD([[subQ2,-1.0]])],"derivedFrom":subQ1}),1.0]])]});}
            var Q20;
            {var subQ0=sQuery(id+"F2.wireOp",EDGE,"E5");var subQ1=sQuery(id+"F2.wireOp",EDGE,"E4");var subQ2=makeQuery(id+"F2.imprint","INTERSECT",VERTEX,{"disambiguationData":[OD(0.0)],"derivedFrom":[subQ1,subQ0]});Q20=makeQuery(id+"F2.imprint","IMPRINT",FACE,{"disambiguationData":[TD([[makeQuery(id+"F2.imprint","IMPRINT",EDGE,{"disambiguationData":[TD([[subQ2,-1.0]])],"derivedFrom":subQ1}),1.0]])]});}
            var Q21;
            {var subQ0=sQuery(id+"F2.wireOp",EDGE,"E5");var subQ1=sQuery(id+"F2.wireOp",EDGE,"E3");var subQ2=makeQuery(id+"F2.imprint","INTERSECT",VERTEX,{"disambiguationData":[OD(1.0)],"derivedFrom":[subQ1,subQ0]});Q21=makeQuery(id+"F2.imprint","IMPRINT",FACE,{"disambiguationData":[TD([[makeQuery(id+"F2.imprint","IMPRINT",EDGE,{"disambiguationData":[TD([[subQ2,1.0]])],"derivedFrom":subQ1}),-1.0]])]});}
            var Q22;
            {var subQ0=sQuery(id+"F2.wireOp",EDGE,"E4");var subQ1=sQuery(id+"F2.wireOp",EDGE,"E2");var subQ2=makeQuery(id+"F2.imprint","INTERSECT",VERTEX,{"disambiguationData":[OD(0.0)],"derivedFrom":[subQ1,subQ0]});Q22=makeQuery(id+"F2.imprint","IMPRINT",FACE,{"disambiguationData":[TD([[makeQuery(id+"F2.imprint","IMPRINT",EDGE,{"disambiguationData":[TD([[subQ2,-1.0]])],"derivedFrom":subQ1}),-1.0]])]});}
            var Q23;
            {var subQ0=sQuery(id+"F2.wireOp",EDGE,"E4");var subQ1=sQuery(id+"F2.wireOp",EDGE,"E2");var subQ2=makeQuery(id+"F2.imprint","INTERSECT",VERTEX,{"disambiguationData":[OD(1.0)],"derivedFrom":[subQ1,subQ0]});Q23=makeQuery(id+"F2.imprint","IMPRINT",FACE,{"disambiguationData":[TD([[makeQuery(id+"F2.imprint","IMPRINT",EDGE,{"disambiguationData":[TD([[subQ2,1.0]])],"derivedFrom":subQ1}),-1.0]])]});}
            var Q24;
            {var subQ0=sQuery(id+"F2.wireOp",EDGE,"E5");var subQ1=sQuery(id+"F2.wireOp",EDGE,"E2");var subQ2=makeQuery(id+"F2.imprint","INTERSECT",VERTEX,{"disambiguationData":[OD(1.0)],"derivedFrom":[subQ1,subQ0]});Q24=makeQuery(id+"F2.imprint","IMPRINT",FACE,{"disambiguationData":[TD([[makeQuery(id+"F2.imprint","IMPRINT",EDGE,{"disambiguationData":[TD([[subQ2,-1.0]])],"derivedFrom":subQ1}),1.0]])]});}
            var Q25;
            {var subQ0=sQuery(id+"F2.wireOp",EDGE,"E5");var subQ1=sQuery(id+"F2.wireOp",EDGE,"E2");var subQ2=makeQuery(id+"F2.imprint","INTERSECT",VERTEX,{"disambiguationData":[OD(0.0)],"derivedFrom":[subQ1,subQ0]});Q25=makeQuery(id+"F2.imprint","IMPRINT",FACE,{"disambiguationData":[TD([[makeQuery(id+"F2.imprint","IMPRINT",EDGE,{"disambiguationData":[TD([[subQ2,-1.0]])],"derivedFrom":subQ1}),1.0]])]});}
            var Q26;
            {var subQ0=sQuery(id+"F2.wireOp",EDGE,"E5");var subQ1=sQuery(id+"F2.wireOp",EDGE,"E2");var subQ2=makeQuery(id+"F2.imprint","INTERSECT",VERTEX,{"disambiguationData":[OD(0.0)],"derivedFrom":[subQ1,subQ0]});Q26=makeQuery(id+"F2.imprint","IMPRINT",FACE,{"disambiguationData":[TD([[makeQuery(id+"F2.imprint","IMPRINT",EDGE,{"disambiguationData":[TD([[subQ2,-1.0]])],"derivedFrom":subQ1}),-1.0]])]});}
            var Q27;
            {var subQ0=sQuery(id+"F2.wireOp",EDGE,"E9.0");var subQ1=sQuery(id+"F2.wireOp",EDGE,"E3");var subQ2=makeQuery(id+"F2.imprint","INTERSECT",VERTEX,{"disambiguationData":[OD(0.0)],"derivedFrom":[subQ1,subQ0]});Q27=makeQuery(id+"F2.imprint","IMPRINT",FACE,{"disambiguationData":[TD([[makeQuery(id+"F2.imprint","IMPRINT",EDGE,{"disambiguationData":[TD([[subQ2,-1.0]])],"derivedFrom":subQ1}),1.0]])]});}
            var Q28;
            {var subQ0=sQuery(id+"F2.wireOp",EDGE,"E9.0");var subQ1=sQuery(id+"F2.wireOp",EDGE,"E3");var subQ2=makeQuery(id+"F2.imprint","INTERSECT",VERTEX,{"disambiguationData":[OD(1.0)],"derivedFrom":[subQ1,subQ0]});Q28=makeQuery(id+"F2.imprint","IMPRINT",FACE,{"disambiguationData":[TD([[makeQuery(id+"F2.imprint","IMPRINT",EDGE,{"disambiguationData":[TD([[subQ2,-1.0]])],"derivedFrom":subQ1}),1.0]])]});}
            var Q29;
            {var subQ0=sQuery(id+"F2.wireOp",EDGE,"E4");var subQ1=sQuery(id+"F2.wireOp",EDGE,"E3");var subQ2=makeQuery(id+"F2.imprint","INTERSECT",VERTEX,{"disambiguationData":[OD(1.0)],"derivedFrom":[subQ1,subQ0]});Q29=makeQuery(id+"F2.imprint","IMPRINT",FACE,{"disambiguationData":[TD([[makeQuery(id+"F2.imprint","IMPRINT",EDGE,{"disambiguationData":[TD([[subQ2,-1.0]])],"derivedFrom":subQ1}),1.0]])]});}
            var Q30;
            {var subQ0=sQuery(id+"F2.wireOp",EDGE,"E7.0");var subQ1=sQuery(id+"F2.wireOp",EDGE,"E4");var subQ2=makeQuery(id+"F2.imprint","INTERSECT",VERTEX,{"disambiguationData":[OD(0.0)],"derivedFrom":[subQ1,subQ0]});Q30=makeQuery(id+"F2.imprint","IMPRINT",FACE,{"disambiguationData":[TD([[makeQuery(id+"F2.imprint","IMPRINT",EDGE,{"disambiguationData":[TD([[subQ2,-1.0]])],"derivedFrom":subQ1}),1.0]])]});}
            var Q31;
            {var subQ0=sQuery(id+"F2.wireOp",EDGE,"E4");var subQ1=sQuery(id+"F2.wireOp",EDGE,"E3");var subQ2=makeQuery(id+"F2.imprint","INTERSECT",VERTEX,{"disambiguationData":[OD(0.0)],"derivedFrom":[subQ1,subQ0]});Q31=makeQuery(id+"F2.imprint","IMPRINT",FACE,{"disambiguationData":[TD([[makeQuery(id+"F2.imprint","IMPRINT",EDGE,{"disambiguationData":[TD([[subQ2,-1.0]])],"derivedFrom":subQ1}),1.0]])]});}
            var Q32;
            {var subQ0=sQuery(id+"F2.wireOp",EDGE,"E4");var subQ1=sQuery(id+"F2.wireOp",EDGE,"E3");var subQ2=makeQuery(id+"F2.imprint","INTERSECT",VERTEX,{"disambiguationData":[OD(0.0)],"derivedFrom":[subQ1,subQ0]});Q32=makeQuery(id+"F2.imprint","IMPRINT",FACE,{"disambiguationData":[TD([[makeQuery(id+"F2.imprint","IMPRINT",EDGE,{"disambiguationData":[TD([[subQ2,-1.0]])],"derivedFrom":subQ1}),-1.0]])]});}
            var Q33;
            {var subQ0=sQuery(id+"F2.wireOp",EDGE,"E5");var subQ1=sQuery(id+"F2.wireOp",EDGE,"E1");var subQ2=makeQuery(id+"F2.imprint","INTERSECT",VERTEX,{"disambiguationData":[OD(0.0)],"derivedFrom":[subQ1,subQ0]});Q33=makeQuery(id+"F2.imprint","IMPRINT",FACE,{"disambiguationData":[TD([[makeQuery(id+"F2.imprint","IMPRINT",EDGE,{"disambiguationData":[TD([[subQ2,-1.0]])],"derivedFrom":subQ1}),-1.0]])]});}
            var Q34;
            {var subQ0=sQuery(id+"F2.wireOp",EDGE,"E5");var subQ1=sQuery(id+"F2.wireOp",EDGE,"E1");var subQ2=makeQuery(id+"F2.imprint","INTERSECT",VERTEX,{"disambiguationData":[OD(0.0)],"derivedFrom":[subQ1,subQ0]});Q34=makeQuery(id+"F2.imprint","IMPRINT",FACE,{"disambiguationData":[TD([[makeQuery(id+"F2.imprint","IMPRINT",EDGE,{"disambiguationData":[TD([[subQ2,-1.0]])],"derivedFrom":subQ1}),1.0]])]});}
            var Q35;
            {var subQ0=sQuery(id+"F2.wireOp",EDGE,"E5");var subQ1=sQuery(id+"F2.wireOp",EDGE,"E1");var subQ2=makeQuery(id+"F2.imprint","INTERSECT",VERTEX,{"disambiguationData":[OD(1.0)],"derivedFrom":[subQ1,subQ0]});Q35=makeQuery(id+"F2.imprint","IMPRINT",FACE,{"disambiguationData":[TD([[makeQuery(id+"F2.imprint","IMPRINT",EDGE,{"disambiguationData":[TD([[subQ2,-1.0]])],"derivedFrom":subQ1}),1.0]])]});}
            var Q36;
            {var subQ0=sQuery(id+"F2.wireOp",EDGE,"E9.0");var subQ1=sQuery(id+"F2.wireOp",EDGE,"E7.0");var subQ2=makeQuery(id+"F2.imprint","INTERSECT",VERTEX,{"disambiguationData":[OD(0.0)],"derivedFrom":[subQ1,subQ0]});Q36=makeQuery(id+"F2.imprint","IMPRINT",FACE,{"disambiguationData":[TD([[makeQuery(id+"F2.imprint","IMPRINT",EDGE,{"disambiguationData":[TD([[subQ2,-1.0]])],"derivedFrom":subQ1}),1.0]])]});}
            extrude(context, id + "F5", {"entities" : qUnion([Q0, Q1, Q2, Q3, Q4, Q5, Q6, Q7, Q8, Q9, Q10, Q11, Q12, Q13, Q14, Q15, Q16, Q17, Q18, Q19, Q20, Q21, Q22, Q23, Q24, Q25, Q26, Q27, Q28, Q29, Q30, Q31, Q32, Q33, Q34, Q35, Q36]), "operationType" : NewBodyOperationType.ADD, "depth" : (getVariable(context, 'thickness') * 1.5) * mm, "offsetDistance" : 25 * mm});
        }
        {
            var Q0;
            {var subQ0=sQuery(id+"F2.wireOp",EDGE,"E10.0");var subQ1=sQuery(id+"F2.wireOp",EDGE,"E4");var subQ2=makeQuery(id+"F2.imprint","INTERSECT",VERTEX,{"disambiguationData":[OD(0.0)],"derivedFrom":[subQ1,subQ0]});Q0=makeQuery(id+"F5.boolean.opBoolean","SPLIT",FACE,{"disambiguationData":[TD([makeQuery(id+"F5.opExtrude","SWEPT_FACE",FACE,{"disambiguationData":[OSD([subQ1]),TDD([makeQuery(id+"F2.imprint","IMPRINT",EDGE,{"disambiguationData":[TD([[subQ2,-1.0]])],"derivedFrom":subQ1})])]})])],"derivedFrom":makeQuery(id+"F4.opExtrude","CAP_FACE",FACE,{"disambiguationData":[OSD([sQuery(id+"F2.wireOp",EDGE,"E1"),sQuery(id+"F2.wireOp",EDGE,"E2"),sQuery(id+"F2.wireOp",EDGE,"E3"),subQ1,sQuery(id+"F2.wireOp",EDGE,"E5"),sQuery(id+"F2.wireOp",EDGE,"E6.0"),sQuery(id+"F2.wireOp",EDGE,"E7.0"),sQuery(id+"F2.wireOp",EDGE,"E8.0"),sQuery(id+"F2.wireOp",EDGE,"E9.0"),subQ0])],"isStart":false})});}
            var Q1;
            {var subQ0=sQuery(id+"F2.wireOp",EDGE,"E6.0");var subQ1=sQuery(id+"F2.wireOp",EDGE,"E3");var subQ2=makeQuery(id+"F2.imprint","INTERSECT",VERTEX,{"disambiguationData":[OD(0.0)],"derivedFrom":[subQ1,subQ0]});Q1=makeQuery(id+"F5.boolean.opBoolean","SPLIT",FACE,{"disambiguationData":[TD([makeQuery(id+"F5.opExtrude","SWEPT_FACE",FACE,{"disambiguationData":[OSD([subQ1]),TDD([makeQuery(id+"F2.imprint","IMPRINT",EDGE,{"disambiguationData":[TD([[subQ2,-1.0]])],"derivedFrom":subQ1})])]})])],"derivedFrom":makeQuery(id+"F4.opExtrude","CAP_FACE",FACE,{"disambiguationData":[OSD([sQuery(id+"F2.wireOp",EDGE,"E1"),sQuery(id+"F2.wireOp",EDGE,"E2"),subQ1,sQuery(id+"F2.wireOp",EDGE,"E4"),sQuery(id+"F2.wireOp",EDGE,"E5"),subQ0,sQuery(id+"F2.wireOp",EDGE,"E7.0"),sQuery(id+"F2.wireOp",EDGE,"E8.0"),sQuery(id+"F2.wireOp",EDGE,"E9.0"),sQuery(id+"F2.wireOp",EDGE,"E10.0")])],"isStart":false})});}
            var Q2;
            {var subQ0=sQuery(id+"F2.wireOp",EDGE,"E5");var subQ1=sQuery(id+"F2.wireOp",EDGE,"E2");var subQ2=makeQuery(id+"F2.imprint","INTERSECT",VERTEX,{"disambiguationData":[OD(1.0)],"derivedFrom":[subQ1,subQ0]});var subQ3=sQuery(id+"F2.wireOp",EDGE,"E9.0");Q2=makeQuery(id+"F5.boolean.opBoolean","SPLIT",FACE,{"disambiguationData":[TD([makeQuery(id+"F5.opExtrude","SWEPT_FACE",FACE,{"disambiguationData":[OSD([subQ1]),TDD([makeQuery(id+"F2.imprint","IMPRINT",EDGE,{"disambiguationData":[TD([[subQ2,-1.0]])],"derivedFrom":subQ1})])]})])],"derivedFrom":makeQuery(id+"F4.opExtrude","CAP_FACE",FACE,{"disambiguationData":[OSD([sQuery(id+"F2.wireOp",EDGE,"E1"),subQ1,sQuery(id+"F2.wireOp",EDGE,"E3"),sQuery(id+"F2.wireOp",EDGE,"E4"),subQ0,sQuery(id+"F2.wireOp",EDGE,"E6.0"),sQuery(id+"F2.wireOp",EDGE,"E7.0"),sQuery(id+"F2.wireOp",EDGE,"E8.0"),subQ3,sQuery(id+"F2.wireOp",EDGE,"E10.0")])],"isStart":false})});}
            var Q3;
            {var subQ0=sQuery(id+"F2.wireOp",EDGE,"E9.0");var subQ1=sQuery(id+"F2.wireOp",EDGE,"E2");var subQ2=makeQuery(id+"F2.imprint","INTERSECT",VERTEX,{"disambiguationData":[OD(0.0)],"derivedFrom":[subQ1,subQ0]});var subQ3=sQuery(id+"F2.wireOp",EDGE,"E5");Q3=makeQuery(id+"F5.boolean.opBoolean","SPLIT",FACE,{"disambiguationData":[TD([makeQuery(id+"F5.opExtrude","SWEPT_FACE",FACE,{"disambiguationData":[OSD([subQ1]),TDD([makeQuery(id+"F2.imprint","IMPRINT",EDGE,{"disambiguationData":[TD([[subQ2,-1.0]])],"derivedFrom":subQ1})])]})])],"derivedFrom":makeQuery(id+"F4.opExtrude","CAP_FACE",FACE,{"disambiguationData":[OSD([sQuery(id+"F2.wireOp",EDGE,"E1"),subQ1,sQuery(id+"F2.wireOp",EDGE,"E3"),sQuery(id+"F2.wireOp",EDGE,"E4"),subQ3,sQuery(id+"F2.wireOp",EDGE,"E6.0"),sQuery(id+"F2.wireOp",EDGE,"E7.0"),sQuery(id+"F2.wireOp",EDGE,"E8.0"),subQ0,sQuery(id+"F2.wireOp",EDGE,"E10.0")])],"isStart":false})});}
            var Q4;
            {var subQ0=sQuery(id+"F2.wireOp",EDGE,"E4");var subQ1=sQuery(id+"F2.wireOp",EDGE,"E3");var subQ2=makeQuery(id+"F2.imprint","INTERSECT",VERTEX,{"disambiguationData":[OD(1.0)],"derivedFrom":[subQ1,subQ0]});var subQ3=sQuery(id+"F2.wireOp",EDGE,"E8.0");Q4=makeQuery(id+"F5.boolean.opBoolean","SPLIT",FACE,{"disambiguationData":[TD([makeQuery(id+"F5.opExtrude","SWEPT_FACE",FACE,{"disambiguationData":[OSD([subQ1]),TDD([makeQuery(id+"F2.imprint","IMPRINT",EDGE,{"disambiguationData":[TD([[subQ2,-1.0]])],"derivedFrom":subQ1})])]})])],"derivedFrom":makeQuery(id+"F4.opExtrude","CAP_FACE",FACE,{"disambiguationData":[OSD([sQuery(id+"F2.wireOp",EDGE,"E1"),sQuery(id+"F2.wireOp",EDGE,"E2"),subQ1,subQ0,sQuery(id+"F2.wireOp",EDGE,"E5"),sQuery(id+"F2.wireOp",EDGE,"E6.0"),sQuery(id+"F2.wireOp",EDGE,"E7.0"),subQ3,sQuery(id+"F2.wireOp",EDGE,"E9.0"),sQuery(id+"F2.wireOp",EDGE,"E10.0")])],"isStart":false})});}
            var Q5;
            {var subQ0=sQuery(id+"F2.wireOp",EDGE,"E5");var subQ1=sQuery(id+"F2.wireOp",EDGE,"E1");var subQ2=makeQuery(id+"F2.imprint","INTERSECT",VERTEX,{"disambiguationData":[OD(1.0)],"derivedFrom":[subQ1,subQ0]});var subQ3=sQuery(id+"F2.wireOp",EDGE,"E7.0");Q5=makeQuery(id+"F5.boolean.opBoolean","SPLIT",FACE,{"disambiguationData":[TD([makeQuery(id+"F5.opExtrude","SWEPT_FACE",FACE,{"disambiguationData":[OSD([subQ1]),TDD([makeQuery(id+"F2.imprint","IMPRINT",EDGE,{"disambiguationData":[TD([[subQ2,-1.0]])],"derivedFrom":subQ1})])]})])],"derivedFrom":makeQuery(id+"F4.opExtrude","CAP_FACE",FACE,{"disambiguationData":[OSD([subQ1,sQuery(id+"F2.wireOp",EDGE,"E2"),sQuery(id+"F2.wireOp",EDGE,"E3"),sQuery(id+"F2.wireOp",EDGE,"E4"),subQ0,sQuery(id+"F2.wireOp",EDGE,"E6.0"),subQ3,sQuery(id+"F2.wireOp",EDGE,"E8.0"),sQuery(id+"F2.wireOp",EDGE,"E9.0"),sQuery(id+"F2.wireOp",EDGE,"E10.0")])],"isStart":false})});}
            var Q6;
            {var subQ0=sQuery(id+"F2.wireOp",EDGE,"E7.0");var subQ1=sQuery(id+"F2.wireOp",EDGE,"E1");var subQ2=makeQuery(id+"F2.imprint","INTERSECT",VERTEX,{"disambiguationData":[OD(0.0)],"derivedFrom":[subQ1,subQ0]});var subQ3=sQuery(id+"F2.wireOp",EDGE,"E5");Q6=makeQuery(id+"F5.boolean.opBoolean","SPLIT",FACE,{"disambiguationData":[TD([makeQuery(id+"F5.opExtrude","SWEPT_FACE",FACE,{"disambiguationData":[OSD([subQ1]),TDD([makeQuery(id+"F2.imprint","IMPRINT",EDGE,{"disambiguationData":[TD([[subQ2,-1.0]])],"derivedFrom":subQ1})])]})])],"derivedFrom":makeQuery(id+"F4.opExtrude","CAP_FACE",FACE,{"disambiguationData":[OSD([subQ1,sQuery(id+"F2.wireOp",EDGE,"E2"),sQuery(id+"F2.wireOp",EDGE,"E3"),sQuery(id+"F2.wireOp",EDGE,"E4"),subQ3,sQuery(id+"F2.wireOp",EDGE,"E6.0"),subQ0,sQuery(id+"F2.wireOp",EDGE,"E8.0"),sQuery(id+"F2.wireOp",EDGE,"E9.0"),sQuery(id+"F2.wireOp",EDGE,"E10.0")])],"isStart":false})});}
            var Q7;
            {var subQ0=sQuery(id+"F2.wireOp",EDGE,"E8.0");var subQ1=sQuery(id+"F2.wireOp",EDGE,"E3");var subQ2=makeQuery(id+"F2.imprint","INTERSECT",VERTEX,{"disambiguationData":[OD(0.0)],"derivedFrom":[subQ1,subQ0]});var subQ3=sQuery(id+"F2.wireOp",EDGE,"E4");Q7=makeQuery(id+"F5.boolean.opBoolean","SPLIT",FACE,{"disambiguationData":[TD([makeQuery(id+"F5.opExtrude","SWEPT_FACE",FACE,{"disambiguationData":[OSD([subQ1]),TDD([makeQuery(id+"F2.imprint","IMPRINT",EDGE,{"disambiguationData":[TD([[subQ2,-1.0]])],"derivedFrom":subQ1})])]})])],"derivedFrom":makeQuery(id+"F4.opExtrude","CAP_FACE",FACE,{"disambiguationData":[OSD([sQuery(id+"F2.wireOp",EDGE,"E1"),sQuery(id+"F2.wireOp",EDGE,"E2"),subQ1,subQ3,sQuery(id+"F2.wireOp",EDGE,"E5"),sQuery(id+"F2.wireOp",EDGE,"E6.0"),sQuery(id+"F2.wireOp",EDGE,"E7.0"),subQ0,sQuery(id+"F2.wireOp",EDGE,"E9.0"),sQuery(id+"F2.wireOp",EDGE,"E10.0")])],"isStart":false})});}
            var Q8;
            {var subQ0=sQuery(id+"F2.wireOp",EDGE,"E10.0");var subQ1=sQuery(id+"F2.wireOp",EDGE,"E9.0");Q8=makeQuery(id+"F5.opExtrude","CAP_EDGE",EDGE,{"disambiguationData":[OSD([subQ1]),TDD([makeQuery(id+"F2.imprint","IMPRINT",EDGE,{"disambiguationData":[TD([[makeQuery(id+"F2.imprint","INTERSECT",VERTEX,{"disambiguationData":[OD(0.0)],"derivedFrom":[subQ1,subQ0]}),-1.0]])],"derivedFrom":subQ1})])],"isStart":false});}
            var Q9;
            {var subQ0=sQuery(id+"F2.wireOp",EDGE,"E10.0");var subQ1=sQuery(id+"F2.wireOp",EDGE,"E5");var subQ2=makeQuery(id+"F2.imprint","INTERSECT",VERTEX,{"disambiguationData":[OD(0.0)],"derivedFrom":[subQ1,subQ0]});var subQ4=makeQuery(id+"F2.imprint","INTERSECT",VERTEX,{"disambiguationData":[OD(1.0)],"derivedFrom":[subQ1,subQ0]});Q9=makeQuery(id+"F5.opExtrude","CAP_EDGE",EDGE,{"disambiguationData":[OSD([subQ0]),TDD([makeQuery(id+"F2.imprint","IMPRINT",EDGE,{"disambiguationData":[TD([[subQ4,1.0]])],"derivedFrom":subQ0}),makeQuery(id+"F2.imprint","IMPRINT",EDGE,{"disambiguationData":[TD([[subQ2,1.0]])],"derivedFrom":subQ0}),makeQuery(id+"F2.imprint","IMPRINT",EDGE,{"disambiguationData":[TD([[subQ2,-1.0]])],"derivedFrom":subQ0})])],"isStart":false});}
            var Q10;
            {var subQ0=sQuery(id+"F2.wireOp",EDGE,"E8.0");var subQ1=sQuery(id+"F2.wireOp",EDGE,"E2");var subQ2=makeQuery(id+"F2.imprint","INTERSECT",VERTEX,{"disambiguationData":[OD(0.0)],"derivedFrom":[subQ1,subQ0]});var subQ4=makeQuery(id+"F2.imprint","INTERSECT",VERTEX,{"disambiguationData":[OD(1.0)],"derivedFrom":[subQ1,subQ0]});Q10=makeQuery(id+"F5.opExtrude","CAP_EDGE",EDGE,{"disambiguationData":[OSD([subQ0]),TDD([makeQuery(id+"F2.imprint","IMPRINT",EDGE,{"disambiguationData":[TD([[subQ4,1.0]])],"derivedFrom":subQ0}),makeQuery(id+"F2.imprint","IMPRINT",EDGE,{"disambiguationData":[TD([[subQ2,1.0]])],"derivedFrom":subQ0}),makeQuery(id+"F2.imprint","IMPRINT",EDGE,{"disambiguationData":[TD([[subQ2,-1.0]])],"derivedFrom":subQ0})])],"isStart":false});}
            var Q11;
            {var subQ0=sQuery(id+"F2.wireOp",EDGE,"E9.0");Q11=makeQuery(id+"F5.opExtrude","CAP_EDGE",EDGE,{"disambiguationData":[OSD([subQ0]),TDD([makeQuery(id+"F2.imprint","IMPRINT",EDGE,{"disambiguationData":[TD([[makeQuery(id+"F2.imprint","INTERSECT",VERTEX,{"disambiguationData":[OD(0.0)],"derivedFrom":[sQuery(id+"F2.wireOp",EDGE,"E3"),subQ0]}),-1.0]])],"derivedFrom":subQ0})])],"isStart":false});}
            var Q12;
            {var subQ0=sQuery(id+"F2.wireOp",EDGE,"E9.0");var subQ1=sQuery(id+"F2.wireOp",EDGE,"E3");Q12=makeQuery(id+"F5.opExtrude","CAP_EDGE",EDGE,{"disambiguationData":[OSD([subQ1]),TDD([makeQuery(id+"F2.imprint","IMPRINT",EDGE,{"disambiguationData":[TD([[makeQuery(id+"F2.imprint","INTERSECT",VERTEX,{"disambiguationData":[OD(0.0)],"derivedFrom":[subQ1,subQ0]}),-1.0]])],"derivedFrom":subQ1})])],"isStart":false});}
            var Q13;
            {var subQ0=sQuery(id+"F2.wireOp",EDGE,"E9.0");Q13=makeQuery(id+"F5.opExtrude","CAP_EDGE",EDGE,{"disambiguationData":[OSD([subQ0]),TDD([makeQuery(id+"F2.imprint","IMPRINT",EDGE,{"disambiguationData":[TD([[makeQuery(id+"F2.imprint","INTERSECT",VERTEX,{"disambiguationData":[OD(1.0)],"derivedFrom":[sQuery(id+"F2.wireOp",EDGE,"E3"),subQ0]}),1.0]])],"derivedFrom":subQ0})])],"isStart":false});}
            var Q14;
            {var subQ0=sQuery(id+"F2.wireOp",EDGE,"E7.0");Q14=makeQuery(id+"F5.opExtrude","CAP_EDGE",EDGE,{"disambiguationData":[OSD([subQ0]),TDD([makeQuery(id+"F2.imprint","IMPRINT",EDGE,{"disambiguationData":[TD([[makeQuery(id+"F2.imprint","INTERSECT",VERTEX,{"disambiguationData":[OD(0.0)],"derivedFrom":[sQuery(id+"F2.wireOp",EDGE,"E4"),subQ0]}),-1.0]])],"derivedFrom":subQ0})])],"isStart":false});}
            var Q15;
            {var subQ0=sQuery(id+"F2.wireOp",EDGE,"E7.0");var subQ1=sQuery(id+"F2.wireOp",EDGE,"E4");Q15=makeQuery(id+"F5.opExtrude","CAP_EDGE",EDGE,{"disambiguationData":[OSD([subQ1]),TDD([makeQuery(id+"F2.imprint","IMPRINT",EDGE,{"disambiguationData":[TD([[makeQuery(id+"F2.imprint","INTERSECT",VERTEX,{"disambiguationData":[OD(0.0)],"derivedFrom":[subQ1,subQ0]}),-1.0]])],"derivedFrom":subQ1})])],"isStart":false});}
            var Q16;
            {var subQ0=sQuery(id+"F2.wireOp",EDGE,"E7.0");Q16=makeQuery(id+"F5.opExtrude","CAP_EDGE",EDGE,{"disambiguationData":[OSD([subQ0]),TDD([makeQuery(id+"F2.imprint","IMPRINT",EDGE,{"disambiguationData":[TD([[makeQuery(id+"F2.imprint","INTERSECT",VERTEX,{"disambiguationData":[OD(1.0)],"derivedFrom":[sQuery(id+"F2.wireOp",EDGE,"E4"),subQ0]}),1.0]])],"derivedFrom":subQ0})])],"isStart":false});}
            var Q17;
            {var subQ0=sQuery(id+"F2.wireOp",EDGE,"E8.0");var subQ1=sQuery(id+"F2.wireOp",EDGE,"E1");var subQ2=makeQuery(id+"F2.imprint","INTERSECT",VERTEX,{"disambiguationData":[OD(0.0)],"derivedFrom":[subQ1,subQ0]});var subQ4=makeQuery(id+"F2.imprint","INTERSECT",VERTEX,{"disambiguationData":[OD(1.0)],"derivedFrom":[subQ1,subQ0]});Q17=makeQuery(id+"F5.opExtrude","CAP_EDGE",EDGE,{"disambiguationData":[OSD([subQ0]),TDD([makeQuery(id+"F2.imprint","IMPRINT",EDGE,{"disambiguationData":[TD([[subQ4,1.0]])],"derivedFrom":subQ0}),makeQuery(id+"F2.imprint","IMPRINT",EDGE,{"disambiguationData":[TD([[subQ2,1.0]])],"derivedFrom":subQ0}),makeQuery(id+"F2.imprint","IMPRINT",EDGE,{"disambiguationData":[TD([[subQ2,-1.0]])],"derivedFrom":subQ0})])],"isStart":false});}
            var Q18;
            {var subQ0=sQuery(id+"F2.wireOp",EDGE,"E6.0");var subQ1=sQuery(id+"F2.wireOp",EDGE,"E5");var subQ2=makeQuery(id+"F2.imprint","INTERSECT",VERTEX,{"disambiguationData":[OD(0.0)],"derivedFrom":[subQ1,subQ0]});var subQ4=makeQuery(id+"F2.imprint","INTERSECT",VERTEX,{"disambiguationData":[OD(1.0)],"derivedFrom":[subQ1,subQ0]});Q18=makeQuery(id+"F5.opExtrude","CAP_EDGE",EDGE,{"disambiguationData":[OSD([subQ0]),TDD([makeQuery(id+"F2.imprint","IMPRINT",EDGE,{"disambiguationData":[TD([[subQ4,1.0]])],"derivedFrom":subQ0}),makeQuery(id+"F2.imprint","IMPRINT",EDGE,{"disambiguationData":[TD([[subQ2,1.0]])],"derivedFrom":subQ0}),makeQuery(id+"F2.imprint","IMPRINT",EDGE,{"disambiguationData":[TD([[subQ2,-1.0]])],"derivedFrom":subQ0})])],"isStart":false});}
            var Q19;
            {var subQ0=sQuery(id+"F2.wireOp",EDGE,"E7.0");var subQ1=sQuery(id+"F2.wireOp",EDGE,"E6.0");Q19=makeQuery(id+"F5.opExtrude","CAP_EDGE",EDGE,{"disambiguationData":[OSD([subQ0]),TDD([makeQuery(id+"F2.imprint","IMPRINT",EDGE,{"disambiguationData":[TD([[makeQuery(id+"F2.imprint","INTERSECT",VERTEX,{"disambiguationData":[OD(0.0)],"derivedFrom":[subQ1,subQ0]}),1.0]])],"derivedFrom":subQ0})])],"isStart":false});}
            chamfer(context, id + "F6", {"entities" : qUnion([Q0, Q1, Q2, Q3, Q4, Q5, Q6, Q7, Q8, Q9, Q10, Q11, Q12, Q13, Q14, Q15, Q16, Q17, Q18, Q19]), "width" : (getVariable(context, 'thickness') * .3) * mm, "tangentPropagation" : true});
        }
        {
            var Q0;
            {var subQ0=sQuery(id+"F2.wireOp",EDGE,"E7.0");var subQ1=sQuery(id+"F2.wireOp",EDGE,"E6.0");Q0=makeQuery(id+"F4.opExtrude","CAP_EDGE",EDGE,{"disambiguationData":[OSD([subQ0]),TDD([makeQuery(id+"F2.imprint","IMPRINT",EDGE,{"disambiguationData":[TD([[makeQuery(id+"F2.imprint","INTERSECT",VERTEX,{"disambiguationData":[OD(0.0)],"derivedFrom":[subQ1,subQ0]}),1.0]])],"derivedFrom":subQ0})])],"isStart":true});}
            var Q1;
            Q1=makeQuery(id+"F4.opExtrude","CAP_EDGE",EDGE,{"disambiguationData":[OSD([sQuery(id+"F2.wireOp",EDGE,"E6.0")])],"isStart":true});
            var Q2;
            {var subQ0=sQuery(id+"F2.wireOp",EDGE,"E8.0");var subQ1=sQuery(id+"F2.wireOp",EDGE,"E1");var subQ2=makeQuery(id+"F2.imprint","INTERSECT",VERTEX,{"disambiguationData":[OD(0.0)],"derivedFrom":[subQ1,subQ0]});var subQ4=makeQuery(id+"F2.imprint","INTERSECT",VERTEX,{"disambiguationData":[OD(1.0)],"derivedFrom":[subQ1,subQ0]});Q2=makeQuery(id+"F4.opExtrude","CAP_EDGE",EDGE,{"disambiguationData":[OSD([subQ0]),TDD([makeQuery(id+"F2.imprint","IMPRINT",EDGE,{"disambiguationData":[TD([[subQ4,1.0]])],"derivedFrom":subQ0}),makeQuery(id+"F2.imprint","IMPRINT",EDGE,{"disambiguationData":[TD([[subQ2,1.0]])],"derivedFrom":subQ0}),makeQuery(id+"F2.imprint","IMPRINT",EDGE,{"disambiguationData":[TD([[subQ2,-1.0]])],"derivedFrom":subQ0})])],"isStart":true});}
            var Q3;
            {var subQ0=sQuery(id+"F2.wireOp",EDGE,"E7.0");var subQ1=sQuery(id+"F2.wireOp",EDGE,"E4");Q3=makeQuery(id+"F4.opExtrude","CAP_EDGE",EDGE,{"disambiguationData":[OSD([subQ1]),TDD([makeQuery(id+"F2.imprint","IMPRINT",EDGE,{"disambiguationData":[TD([[makeQuery(id+"F2.imprint","INTERSECT",VERTEX,{"disambiguationData":[OD(0.0)],"derivedFrom":[subQ1,subQ0]}),-1.0]])],"derivedFrom":subQ1})])],"isStart":true});}
            var Q4;
            {var subQ0=sQuery(id+"F2.wireOp",EDGE,"E7.0");Q4=makeQuery(id+"F4.opExtrude","CAP_EDGE",EDGE,{"disambiguationData":[OSD([subQ0]),TDD([makeQuery(id+"F2.imprint","IMPRINT",EDGE,{"disambiguationData":[TD([[makeQuery(id+"F2.imprint","INTERSECT",VERTEX,{"disambiguationData":[OD(1.0)],"derivedFrom":[sQuery(id+"F2.wireOp",EDGE,"E4"),subQ0]}),1.0]])],"derivedFrom":subQ0})])],"isStart":true});}
            var Q5;
            {var subQ0=sQuery(id+"F2.wireOp",EDGE,"E7.0");Q5=makeQuery(id+"F4.opExtrude","CAP_EDGE",EDGE,{"disambiguationData":[OSD([subQ0]),TDD([makeQuery(id+"F2.imprint","IMPRINT",EDGE,{"disambiguationData":[TD([[makeQuery(id+"F2.imprint","INTERSECT",VERTEX,{"disambiguationData":[OD(0.0)],"derivedFrom":[sQuery(id+"F2.wireOp",EDGE,"E4"),subQ0]}),-1.0]])],"derivedFrom":subQ0})])],"isStart":true});}
            var Q6;
            {var subQ0=sQuery(id+"F2.wireOp",EDGE,"E9.0");Q6=makeQuery(id+"F4.opExtrude","CAP_EDGE",EDGE,{"disambiguationData":[OSD([subQ0]),TDD([makeQuery(id+"F2.imprint","IMPRINT",EDGE,{"disambiguationData":[TD([[makeQuery(id+"F2.imprint","INTERSECT",VERTEX,{"disambiguationData":[OD(1.0)],"derivedFrom":[sQuery(id+"F2.wireOp",EDGE,"E3"),subQ0]}),1.0]])],"derivedFrom":subQ0})])],"isStart":true});}
            var Q7;
            {var subQ0=sQuery(id+"F2.wireOp",EDGE,"E9.0");var subQ1=sQuery(id+"F2.wireOp",EDGE,"E3");Q7=makeQuery(id+"F4.opExtrude","CAP_EDGE",EDGE,{"disambiguationData":[OSD([subQ1]),TDD([makeQuery(id+"F2.imprint","IMPRINT",EDGE,{"disambiguationData":[TD([[makeQuery(id+"F2.imprint","INTERSECT",VERTEX,{"disambiguationData":[OD(0.0)],"derivedFrom":[subQ1,subQ0]}),-1.0]])],"derivedFrom":subQ1})])],"isStart":true});}
            var Q8;
            {var subQ0=sQuery(id+"F2.wireOp",EDGE,"E9.0");Q8=makeQuery(id+"F4.opExtrude","CAP_EDGE",EDGE,{"disambiguationData":[OSD([subQ0]),TDD([makeQuery(id+"F2.imprint","IMPRINT",EDGE,{"disambiguationData":[TD([[makeQuery(id+"F2.imprint","INTERSECT",VERTEX,{"disambiguationData":[OD(0.0)],"derivedFrom":[sQuery(id+"F2.wireOp",EDGE,"E3"),subQ0]}),-1.0]])],"derivedFrom":subQ0})])],"isStart":true});}
            var Q9;
            {var subQ0=sQuery(id+"F2.wireOp",EDGE,"E8.0");var subQ1=sQuery(id+"F2.wireOp",EDGE,"E2");var subQ2=makeQuery(id+"F2.imprint","INTERSECT",VERTEX,{"disambiguationData":[OD(0.0)],"derivedFrom":[subQ1,subQ0]});var subQ4=makeQuery(id+"F2.imprint","INTERSECT",VERTEX,{"disambiguationData":[OD(1.0)],"derivedFrom":[subQ1,subQ0]});Q9=makeQuery(id+"F4.opExtrude","CAP_EDGE",EDGE,{"disambiguationData":[OSD([subQ0]),TDD([makeQuery(id+"F2.imprint","IMPRINT",EDGE,{"disambiguationData":[TD([[subQ4,1.0]])],"derivedFrom":subQ0}),makeQuery(id+"F2.imprint","IMPRINT",EDGE,{"disambiguationData":[TD([[subQ2,1.0]])],"derivedFrom":subQ0}),makeQuery(id+"F2.imprint","IMPRINT",EDGE,{"disambiguationData":[TD([[subQ2,-1.0]])],"derivedFrom":subQ0})])],"isStart":true});}
            var Q10;
            Q10=makeQuery(id+"F4.opExtrude","CAP_EDGE",EDGE,{"disambiguationData":[OSD([sQuery(id+"F2.wireOp",EDGE,"E10.0")])],"isStart":true});
            var Q11;
            {var subQ0=sQuery(id+"F2.wireOp",EDGE,"E10.0");var subQ1=sQuery(id+"F2.wireOp",EDGE,"E9.0");Q11=makeQuery(id+"F4.opExtrude","CAP_EDGE",EDGE,{"disambiguationData":[OSD([subQ1]),TDD([makeQuery(id+"F2.imprint","IMPRINT",EDGE,{"disambiguationData":[TD([[makeQuery(id+"F2.imprint","INTERSECT",VERTEX,{"disambiguationData":[OD(0.0)],"derivedFrom":[subQ1,subQ0]}),-1.0]])],"derivedFrom":subQ1})])],"isStart":true});}
            chamfer(context, id + "F7", {"entities" : qUnion([Q0, Q1, Q2, Q3, Q4, Q5, Q6, Q7, Q8, Q9, Q10, Q11]), "width" : (getVariable(context, 'thickness') * .4) * mm, "tangentPropagation" : true});
        }
        {
            var Q0;
            {var subQ0=sQuery(id+"F2.wireOp",EDGE,"E3");var subQ1=sQuery(id+"F2.wireOp",EDGE,"E1");var subQ2=makeQuery(id+"F2.imprint","INTERSECT",VERTEX,{"disambiguationData":[OD(0.0)],"derivedFrom":[subQ1,subQ0]});Q0=makeQuery(id+"F5.boolean.opBoolean","MERGE",EDGE,{"derivedFrom":[makeQuery(id+"F4.opExtrude","SWEPT_EDGE",EDGE,{"disambiguationData":[OSD([subQ1,subQ0]),TDD([subQ2])]}),makeQuery(id+"F5.opExtrude","SWEPT_EDGE",EDGE,{"disambiguationData":[OSD([subQ1,subQ0]),TDD([subQ2])]})]});}
            var Q1;
            {var subQ0=sQuery(id+"F2.wireOp",EDGE,"E5");var subQ1=sQuery(id+"F2.wireOp",EDGE,"E3");var subQ2=makeQuery(id+"F2.imprint","INTERSECT",VERTEX,{"disambiguationData":[OD(0.0)],"derivedFrom":[subQ1,subQ0]});Q1=makeQuery(id+"F5.boolean.opBoolean","MERGE",EDGE,{"derivedFrom":[makeQuery(id+"F4.opExtrude","SWEPT_EDGE",EDGE,{"disambiguationData":[OSD([subQ1,subQ0]),TDD([subQ2])]}),makeQuery(id+"F5.opExtrude","SWEPT_EDGE",EDGE,{"disambiguationData":[OSD([subQ1,subQ0]),TDD([subQ2])]})]});}
            var Q2;
            {var subQ0=sQuery(id+"F2.wireOp",EDGE,"E5");var subQ1=sQuery(id+"F2.wireOp",EDGE,"E4");var subQ2=makeQuery(id+"F2.imprint","INTERSECT",VERTEX,{"disambiguationData":[OD(1.0)],"derivedFrom":[subQ1,subQ0]});Q2=makeQuery(id+"F5.boolean.opBoolean","MERGE",EDGE,{"derivedFrom":[makeQuery(id+"F4.opExtrude","SWEPT_EDGE",EDGE,{"disambiguationData":[OSD([subQ1,subQ0]),TDD([subQ2])]}),makeQuery(id+"F5.opExtrude","SWEPT_EDGE",EDGE,{"disambiguationData":[OSD([subQ1,subQ0]),TDD([subQ2])]})]});}
            var Q3;
            {var subQ0=sQuery(id+"F2.wireOp",EDGE,"E4");var subQ1=sQuery(id+"F2.wireOp",EDGE,"E2");var subQ2=makeQuery(id+"F2.imprint","INTERSECT",VERTEX,{"disambiguationData":[OD(1.0)],"derivedFrom":[subQ1,subQ0]});Q3=makeQuery(id+"F5.boolean.opBoolean","MERGE",EDGE,{"derivedFrom":[makeQuery(id+"F4.opExtrude","SWEPT_EDGE",EDGE,{"disambiguationData":[OSD([subQ1,subQ0]),TDD([subQ2])]}),makeQuery(id+"F5.opExtrude","SWEPT_EDGE",EDGE,{"disambiguationData":[OSD([subQ1,subQ0]),TDD([subQ2])]})]});}
            var Q4;
            {var subQ0=sQuery(id+"F2.wireOp",EDGE,"E3");var subQ1=sQuery(id+"F2.wireOp",EDGE,"E1");var subQ2=makeQuery(id+"F2.imprint","INTERSECT",VERTEX,{"disambiguationData":[OD(1.0)],"derivedFrom":[subQ1,subQ0]});Q4=makeQuery(id+"F5.boolean.opBoolean","MERGE",EDGE,{"derivedFrom":[makeQuery(id+"F4.opExtrude","SWEPT_EDGE",EDGE,{"disambiguationData":[OSD([subQ1,subQ0]),TDD([subQ2])]}),makeQuery(id+"F5.opExtrude","SWEPT_EDGE",EDGE,{"disambiguationData":[OSD([subQ1,subQ0]),TDD([subQ2])]})]});}
            var Q5;
            {var subQ0=sQuery(id+"F2.wireOp",EDGE,"E5");var subQ1=sQuery(id+"F2.wireOp",EDGE,"E3");var subQ2=makeQuery(id+"F2.imprint","INTERSECT",VERTEX,{"disambiguationData":[OD(1.0)],"derivedFrom":[subQ1,subQ0]});Q5=makeQuery(id+"F5.boolean.opBoolean","MERGE",EDGE,{"derivedFrom":[makeQuery(id+"F4.opExtrude","SWEPT_EDGE",EDGE,{"disambiguationData":[OSD([subQ1,subQ0]),TDD([subQ2])]}),makeQuery(id+"F5.opExtrude","SWEPT_EDGE",EDGE,{"disambiguationData":[OSD([subQ1,subQ0]),TDD([subQ2])]})]});}
            var Q6;
            {var subQ0=sQuery(id+"F2.wireOp",EDGE,"E5");var subQ1=sQuery(id+"F2.wireOp",EDGE,"E4");var subQ2=makeQuery(id+"F2.imprint","INTERSECT",VERTEX,{"disambiguationData":[OD(0.0)],"derivedFrom":[subQ1,subQ0]});Q6=makeQuery(id+"F5.boolean.opBoolean","MERGE",EDGE,{"derivedFrom":[makeQuery(id+"F4.opExtrude","SWEPT_EDGE",EDGE,{"disambiguationData":[OSD([subQ1,subQ0]),TDD([subQ2])]}),makeQuery(id+"F5.opExtrude","SWEPT_EDGE",EDGE,{"disambiguationData":[OSD([subQ1,subQ0]),TDD([subQ2])]})]});}
            var Q7;
            {var subQ0=sQuery(id+"F2.wireOp",EDGE,"E4");var subQ1=sQuery(id+"F2.wireOp",EDGE,"E2");var subQ2=makeQuery(id+"F2.imprint","INTERSECT",VERTEX,{"disambiguationData":[OD(0.0)],"derivedFrom":[subQ1,subQ0]});Q7=makeQuery(id+"F5.boolean.opBoolean","MERGE",EDGE,{"derivedFrom":[makeQuery(id+"F4.opExtrude","SWEPT_EDGE",EDGE,{"disambiguationData":[OSD([subQ1,subQ0]),TDD([subQ2])]}),makeQuery(id+"F5.opExtrude","SWEPT_EDGE",EDGE,{"disambiguationData":[OSD([subQ1,subQ0]),TDD([subQ2])]})]});}
            fillet(context, id + "F8", {"entities" : qUnion([Q0, Q1, Q2, Q3, Q4, Q5, Q6, Q7]), "radius" : (getVariable(context, 'thickness') * 3) * mm, "tangentPropagation" : true, "allowEdgeOverflow" : false});
        }
        {
            var Q0;
            {var subQ0=sQuery(id+"F2.wireOp",EDGE,"E3");var subQ1=sQuery(id+"F2.wireOp",EDGE,"E1");var subQ2=makeQuery(id+"F2.imprint","INTERSECT",VERTEX,{"disambiguationData":[OD(0.0)],"derivedFrom":[subQ1,subQ0]});var subQ3=makeQuery(id+"F2.imprint","IMPRINT",EDGE,{"disambiguationData":[TD([[subQ2,1.0]])],"derivedFrom":subQ1});Q0=makeQuery(id+"F11.boolean.opBoolean","SPLIT",EDGE,{"disambiguationData":[TD([makeQuery(id+"F8.opFillet","BLEND_FACE",FACE,{"disambiguationData":[OSD([subQ1,subQ0]),TDD([makeQuery(id+"F5.boolean.opBoolean","MERGE",EDGE,{"derivedFrom":[makeQuery(id+"F4.opExtrude","SWEPT_EDGE",EDGE,{"disambiguationData":[OSD([subQ1,subQ0]),TDD([subQ2])]}),makeQuery(id+"F5.opExtrude","SWEPT_EDGE",EDGE,{"disambiguationData":[OSD([subQ1,subQ0]),TDD([subQ2])]})]})])]})])],"derivedFrom":makeQuery(id+"F5.opExtrude","CAP_EDGE",EDGE,{"disambiguationData":[OSD([subQ1]),TDD([subQ3])],"isStart":false})});}
            fillet(context, id + "F9", {"entities" : qUnion([Q0]), "radius" : (getVariable(context, 'thickness') / 2) * mm, "tangentPropagation" : true, "allowEdgeOverflow" : false});
        }
        {
            var Q0;
            {var subQ0=sQuery(id+"F2.wireOp",EDGE,"E3");var subQ1=sQuery(id+"F2.wireOp",EDGE,"E1");Q0=makeQuery(id+"F4.opExtrude","CAP_EDGE",EDGE,{"disambiguationData":[OSD([subQ1]),TDD([makeQuery(id+"F2.imprint","IMPRINT",EDGE,{"disambiguationData":[TD([[makeQuery(id+"F2.imprint","INTERSECT",VERTEX,{"disambiguationData":[OD(0.0)],"derivedFrom":[subQ1,subQ0]}),1.0]])],"derivedFrom":subQ1})])],"isStart":true});}
            chamfer(context, id + "F10", {"entities" : qUnion([Q0]), "width" : (getVariable(context, 'thickness') / 2) * mm, "tangentPropagation" : true});
        }
        {
            var Q0;
            Q0=makeQuery(id+"F3.imprint","IMPRINT",FACE,{"disambiguationData":[TD([[makeQuery(id+"F3.imprint","IMPRINT",EDGE,{"derivedFrom":sQuery(id+"F3.wireOp",EDGE,"E12")}),-1.0]])]});
            extrude(context, id + "F11", {"entities" : qUnion([Q0]), "operationType" : NewBodyOperationType.ADD, "oppositeDirection" : true, "depth" : (getVariable(context, 'handle_length') / 2) * mm, "offsetDistance" : 25 * mm, "hasSecondDirection" : true, "secondDirectionOppositeDirection" : true, "secondDirectionDepth" : (getVariable(context, 'handle_length') / 2 - getVariable(context, 'thickness') * 4) * mm});
        }
        {
            var Q0;
            Q0=makeQuery(id+"F3.imprint","IMPRINT",FACE,{"disambiguationData":[TD([[makeQuery(id+"F3.imprint","IMPRINT",EDGE,{"derivedFrom":sQuery(id+"F3.wireOp",EDGE,"E12")}),1.0]])]});
            extrude(context, id + "F12", {"entities" : qUnion([Q0]), "operationType" : NewBodyOperationType.REMOVE, "oppositeDirection" : true, "depth" : (getVariable(context, 'handle_length') / 2) * mm, "offsetDistance" : 25 * mm, "hasSecondDirection" : true, "secondDirectionOppositeDirection" : true, "secondDirectionDepth" : (getVariable(context, 'handle_length') / 2 - getVariable(context, 'thickness') * 4) * mm});
        }
        {
            var Q0;
            Q0=makeQuery(id+"F11.opExtrude","CAP_EDGE",EDGE,{"disambiguationData":[OSD([sQuery(id+"F3.wireOp",EDGE,"E13.0")])],"isStart":true});
            var Q1;
            Q1=makeQuery(id+"F11.opExtrude","CAP_EDGE",EDGE,{"disambiguationData":[OSD([sQuery(id+"F3.wireOp",EDGE,"E13.0")])],"isStart":false});
            var Q2;
            Q2=makeQuery(id+"F11.opExtrude","CAP_EDGE",EDGE,{"disambiguationData":[OSD([sQuery(id+"F3.wireOp",EDGE,"E12")])],"isStart":false});
            var Q3;
            Q3=makeQuery(id+"F11.opExtrude","CAP_EDGE",EDGE,{"disambiguationData":[OSD([sQuery(id+"F3.wireOp",EDGE,"E12")])],"isStart":true});
            fillet(context, id + "F13", {"entities" : qUnion([Q0, Q1, Q2, Q3]), "radius" : (getVariable(context, 'thickness') / 2) * mm, "tangentPropagation" : true, "allowEdgeOverflow" : false});
        }
    });
